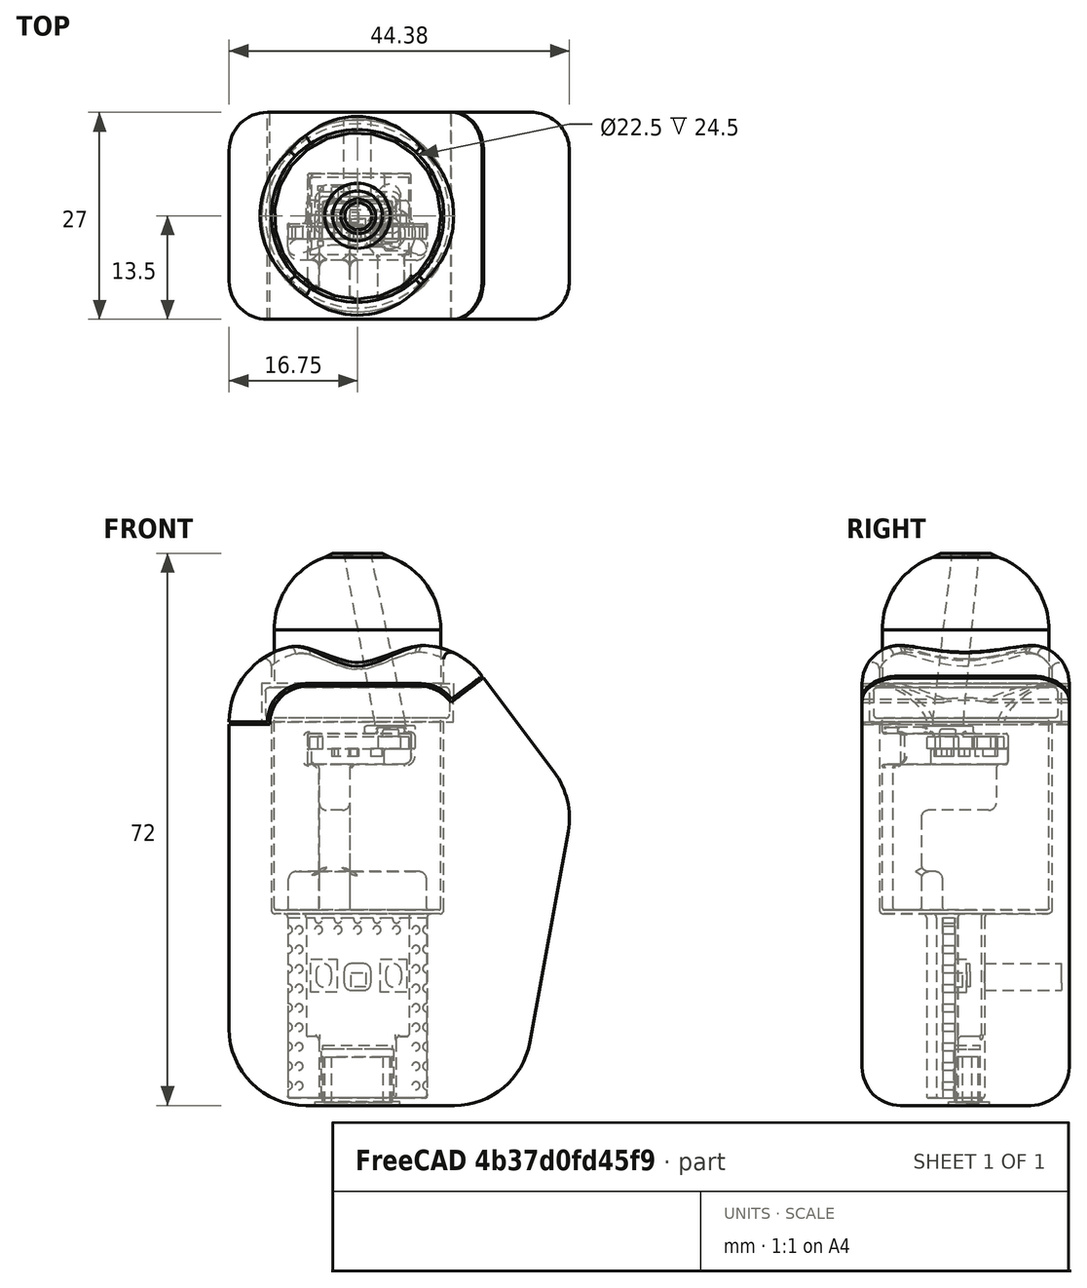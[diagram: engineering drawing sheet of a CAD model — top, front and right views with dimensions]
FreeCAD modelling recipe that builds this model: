
FCSTD DOCUMENT  (FreeCAD 1.0RUnknown)
Label: Device_V7
License: All rights reserved
objects: PartDesign::Fillet×52, Sketcher::SketchObject×37, PartDesign::Pocket×25, PartDesign::Pad×7, PartDesign::SubtractiveLoft×3, PartDesign::Body×3, PartDesign::Revolution×2, Part::Feature×2, PartDesign::SubtractivePipe×1, PartDesign::Groove×1
note: 352 computed .brp shape members not serialized (recipe doc carries the construction recipe); baked Part::Feature solids carry a one-line shape summary decoded from their .brp

FEATURE [Sketcher::SketchObject] Sketch
  ArcFitTolerance = 1e-06
  AttachmentSupport = -> [XZ_Plane]
  FullyConstrained = true
  MakeInternals = false
  MapMode = 5
  Placement = pos=(0,0,0) rot=(1,0,0;1.5708rad)
  sketch-geometry (8):
    g0: LineSegment [constr] StartX=0 StartY=0 StartZ=0 EndX=0 EndY=75 EndZ=0
    g1: LineSegment StartX=0 StartY=75 StartZ=0 EndX=30 EndY=75 EndZ=0
    g2: LineSegment StartX=30 StartY=75 StartZ=0 EndX=45 EndY=55 EndZ=0
    g3: LineSegment [constr] StartX=45 StartY=55 StartZ=0 EndX=35 EndY=0 EndZ=0
    g4: LineSegment [constr] StartX=35 StartY=0 StartZ=0 EndX=0 EndY=0 EndZ=0
    g5: LineSegment StartX=0 StartY=75 StartZ=0 EndX=0 EndY=15 EndZ=0
    g6: LineSegment StartX=0 StartY=15 StartZ=0 EndX=37.7273 EndY=15 EndZ=0
    g7: LineSegment StartX=37.7273 StartY=15 StartZ=0 EndX=45 EndY=55 EndZ=0
  constraints (22):
    c: Coincident(g-1,g0)
    c: Coincident(g0,g1)
    c: Horizontal(g1)
    c: Coincident(g1,g2)
    c: Coincident(g2,g3)
    c: Coincident(g3,g4)
    c: Coincident(g4,g0)
    c: Vertical(g0)
    c: Horizontal(g4)
    c: DistanceX(g4,g4) = 35
    c: DistanceX(g1,g1) = 30
    c: DistanceY(g0,g0) = 75
    c: DistanceY(g2,g1) = 20
    c: DistanceX(g0,g2) = 45
    c: Coincident(g5,g0)
    c: Coincident(g6,g5)
    c: Horizontal(g6)
    c: Coincident(g7,g6)
    c: Coincident(g7,g2)
    c: PointOnObject(g6,g3)
    c: Vertical(g5)
    c: DistanceY(g0,g5) = 15
FEATURE [PartDesign::Pad] Pad
  Direction = (0,-1,2e-16)
  Length = 27
  Length2 = 10
  Midplane = true
  Placement = pos=(0,0,0) rot=(1,0,0;1.5708rad)
  Profile = -> Sketch
  ReferenceAxis = -> Sketch [N_Axis]
  Refine = true
  Suppressed = false
  Type = 0
FEATURE [PartDesign::Fillet] Fillet
  Base = -> Pad [Edge2,Edge5,Edge8,Edge1,Edge11]
  BaseFeature = -> Pad
  Placement = pos=(0,0,0) rot=(1,0,0;1.5708rad)
  Radius = 10
  Refine = true
  SupportTransform = false
  Suppressed = false
  UseAllEdges = false
FEATURE [PartDesign::Fillet] Fillet001
  Base = -> Fillet [Edge19,Edge8]
  BaseFeature = -> Fillet
  Placement = pos=(0,0,0) rot=(1,0,0;1.5708rad)
  Radius = 5
  Refine = true
  SupportTransform = false
  Suppressed = false
  UseAllEdges = false
FEATURE [Sketcher::SketchObject] Sketch003
  ArcFitTolerance = 1e-06
  AttachmentSupport = -> [XZ_Plane001]
  FullyConstrained = true
  MakeInternals = false
  MapMode = 5
  Placement = pos=(0,0,0) rot=(1,0,0;1.5708rad)
  sketch-geometry (9):
    g0: LineSegment StartX=19 StartY=87 StartZ=0 EndX=19 EndY=77 EndZ=0
    g1: LineSegment StartX=19 StartY=77 StartZ=0 EndX=27.6 EndY=77 EndZ=0
    g2: LineSegment StartX=19 StartY=87 StartZ=0 EndX=20 EndY=87 EndZ=0
    g3: LineSegment StartX=20 StartY=87 StartZ=0 EndX=21 EndY=86.5 EndZ=0
    g4: ArcOfCircle CenterX=17.6068 CenterY=77.1 CenterZ=0 NormalX=0 NormalY=0 NormalZ=1 AngleXU=0 Radius=9.99368 StartAngle=6.27318 EndAngle=7.50756
    g5: LineSegment [constr] StartX=0 StartY=0 StartZ=0 EndX=27.6 EndY=0 EndZ=0
    g6: LineSegment [constr] StartX=27.6 StartY=0 StartZ=0 EndX=27.6 EndY=77 EndZ=0
    g7: LineSegment [constr] StartX=27.6 StartY=77 StartZ=0 EndX=0 EndY=77 EndZ=0
    g8: LineSegment [constr] StartX=0 StartY=77 StartZ=0 EndX=0 EndY=0 EndZ=0
  constraints (26):
    c: Vertical(g0)
    c: Coincident(g0,g1)
    c: Horizontal(g1)
    c: Coincident(g0,g2)
    c: Horizontal(g2)
    c: Coincident(g2,g3)
    c: Coincident(g4,g3)
    c: Coincident(g4,g1)
    c: DistanceY(g0,g0) = 10
    c: DistanceY(g3,g2) = 0.5
    c: DistanceX(g2,g2) = 1
    c: DistanceX(g2,g3) = 1
    c: DistanceX(g1,g1) = 8.6
    c: Coincident(g5,g6)
    c: Coincident(g6,g7)
    c: Coincident(g7,g8)
    c: Coincident(g8,g5)
    c: Horizontal(g5)
    c: Horizontal(g7)
    c: Vertical(g6)
    c: Vertical(g8)
    c: Coincident(g5,g-1)
    c: Coincident(g6,g1)
    c: DistanceY(g8,g8) = 77
    c: DistanceX(g7,g7) = 27.6
    c: DistanceY(g0,g4) = 0.1
FEATURE [Sketcher::SketchObject] Sketch004
  ArcFitTolerance = 1e-06
  AttachmentSupport = -> [XZ_Plane001]
  FullyConstrained = true
  MakeInternals = false
  MapMode = 5
  Placement = pos=(0,0,0) rot=(1,0,0;1.5708rad)
  sketch-geometry (7):
    g0: LineSegment StartX=16.75 StartY=87 StartZ=0 EndX=16.75 EndY=77 EndZ=0
    g1: LineSegment [constr] StartX=0 StartY=0 StartZ=0 EndX=27.5 EndY=0 EndZ=0
    g2: LineSegment [constr] StartX=27.5 StartY=0 StartZ=0 EndX=27.5 EndY=77 EndZ=0
    g3: LineSegment [constr] StartX=27.5 StartY=77 StartZ=0 EndX=0 EndY=77 EndZ=0
    g4: LineSegment [constr] StartX=0 StartY=77 StartZ=0 EndX=0 EndY=0 EndZ=0
    g5: GeomPoint [constr] X=10 Y=77 Z=0
    g6: GeomPoint [constr] X=23.5 Y=77 Z=0
  constraints (18):
    c: Vertical(g0)
    c: DistanceY(g0,g0) = 10
    c: Coincident(g1,g2)
    c: Coincident(g2,g3)
    c: Coincident(g3,g4)
    c: Coincident(g4,g1)
    c: Horizontal(g1)
    c: Horizontal(g3)
    c: Vertical(g2)
    c: Vertical(g4)
    c: Coincident(g1,g-1)
    c: DistanceY(g4,g4) = 77
    c: DistanceX(g3,g3) = 27.5
    c: PointOnObject(g5,g3)
    c: PointOnObject(g6,g3)
    c: DistanceX(g6,g2) = 4
    c: DistanceX(g3,g5) = 10
    c: Symmetric(g5,g6,g0)
FEATURE [PartDesign::Revolution] Revolution
  Angle = 360
  Angle2 = 60
  Axis = (0,-2e-16,-1)
  Base = (16.75,1.93e-14,87)
  Placement = pos=(0,0,0) rot=(1,0,0;1.5708rad)
  Profile = -> Sketch003
  ReferenceAxis = -> Sketch004 [Edge1]
  Refine = true
  Reversed = true
  Suppressed = false
  Type = 0
FEATURE [PartDesign::Pad] Pad001
  BaseFeature = -> Revolution
  Direction = (0,-2e-16,-1)
  Length = 36.5
  Length2 = 10
  Placement = pos=(0,0,0) rot=(1,0,0;1.5708rad)
  Profile = -> Revolution [Face2]
  Refine = true
  Suppressed = false
  Type = 0
FEATURE [Sketcher::SketchObject] Sketch006
  ArcFitTolerance = 1e-06
  AttachmentOffset = pos=(0,0,-25) rot=(0,0,1;0rad)
  AttachmentSupport = -> [Fillet001]
  FullyConstrained = true
  MakeInternals = false
  MapMode = 5
  Placement = pos=(0,6.6e-15,40) rot=(1,0,0;3.14159rad)
  sketch-geometry (1):
    g0: Circle CenterX=16.75 CenterY=0 CenterZ=0 NormalX=0 NormalY=0 NormalZ=1 AngleXU=0 Radius=11.25
  constraints (3):
    c: PointOnObject(g0,g-1)
    c: DistanceX(g-1,g0) = 16.75
    c: Diameter(g0) = 22.5
FEATURE [PartDesign::Pocket] Pocket
  BaseFeature = -> Fillet001
  Direction = (0,0,1)
  Length = 5
  Length2 = 5
  Placement = pos=(0,0,0) rot=(1,0,0;1.5708rad)
  Profile = -> Sketch006
  ReferenceAxis = -> Sketch006 [N_Axis]
  Refine = true
  Suppressed = false
  Type = 1
FEATURE [Part::Feature] Part__Feature  label="RP2350-Zero-mini"
  Placement = pos=(7.75,-3,39.5) rot=(1,0,0;4.71239rad)
  shape: bbox 18 x 4.88 x 24.16 mm, 130 faces (baked)
FEATURE [Sketcher::SketchObject] Sketch008
  ArcFitTolerance = 1e-06
  AttachmentSupport = -> [Pocket]
  ExternalGeometry = -> [Pocket]
  FullyConstrained = true
  MakeInternals = false
  MapMode = 5
  Placement = pos=(0,0,40) rot=(0,0,1;3.14159rad)
  sketch-geometry (19):
    g0: LineSegment [constr] StartX=-25.85 StartY=5.5 StartZ=0 EndX=-7.65 EndY=5.5 EndZ=0
    g1: LineSegment StartX=-7.65 StartY=5.5 StartZ=0 EndX=-7.65 EndY=1 EndZ=0
    g2: LineSegment [constr] StartX=-7.65 StartY=1 StartZ=0 EndX=-9.75 EndY=1 EndZ=0
    g3: LineSegment [constr] StartX=-9.75 StartY=1 StartZ=0 EndX=-9.75 EndY=-1.5 EndZ=0
    g4: LineSegment [constr] StartX=-9.75 StartY=-1.5 StartZ=0 EndX=-11.75 EndY=-1.5 EndZ=0
    g5: LineSegment [constr] StartX=-11.75 StartY=-1.5 StartZ=0 EndX=-11.75 EndY=-2.5 EndZ=0
    g6: LineSegment StartX=-11.75 StartY=-2.5 StartZ=0 EndX=-21.75 EndY=-2.5 EndZ=0
    g7: LineSegment [constr] StartX=-21.75 StartY=-2.5 StartZ=0 EndX=-21.75 EndY=-1.5 EndZ=0
    g8: LineSegment [constr] StartX=-21.75 StartY=-1.5 StartZ=0 EndX=-23.75 EndY=-1.5 EndZ=0
    g9: LineSegment [constr] StartX=-23.75 StartY=-1.5 StartZ=0 EndX=-23.75 EndY=1 EndZ=0
    g10: LineSegment [constr] StartX=-23.75 StartY=1 StartZ=0 EndX=-25.85 EndY=1 EndZ=0
    g11: LineSegment StartX=-25.85 StartY=1 StartZ=0 EndX=-25.85 EndY=5.5 EndZ=0
    g12: LineSegment StartX=-25.85 StartY=5.5 StartZ=0 EndX=-20.85 EndY=3.8 EndZ=0
    g13: LineSegment StartX=-20.85 StartY=3.8 StartZ=0 EndX=-12.65 EndY=3.8 EndZ=0
    g14: LineSegment StartX=-12.65 StartY=3.8 StartZ=0 EndX=-7.65 EndY=5.5 EndZ=0
    g15: LineSegment StartX=-25.85 StartY=1 StartZ=0 EndX=-21.75 EndY=1 EndZ=0
    g16: LineSegment StartX=-21.75 StartY=1 StartZ=0 EndX=-21.75 EndY=-2.5 EndZ=0
    g17: LineSegment StartX=-11.75 StartY=-2.5 StartZ=0 EndX=-11.75 EndY=1 EndZ=0
    g18: LineSegment StartX=-11.75 StartY=1 StartZ=0 EndX=-7.65 EndY=1 EndZ=0
  constraints (54):
    c: Horizontal(g0)
    c: Coincident(g0,g1)
    c: Vertical(g1)
    c: Coincident(g1,g2)
    c: Horizontal(g2)
    c: Coincident(g2,g3)
    c: Vertical(g3)
    c: Coincident(g3,g4)
    c: Horizontal(g4)
    c: Coincident(g4,g5)
    c: Vertical(g5)
    c: Coincident(g5,g6)
    c: Horizontal(g6)
    c: Coincident(g6,g7)
    c: Vertical(g7)
    c: Coincident(g7,g8)
    c: Horizontal(g8)
    c: Coincident(g8,g9)
    c: Vertical(g9)
    c: Coincident(g9,g10)
    c: Horizontal(g10)
    c: Coincident(g10,g11)
    c: Vertical(g11)
    c: Coincident(g0,g11)
    c: DistanceX(g0,g-3) = 9.1
    c: DistanceX(g0,g0) = 18.2
    c: DistanceY(g-3,g1) = 1
    c: Horizontal(g2,g9)
    c: DistanceX(g8,g-3) = 7
    c: DistanceX(g-3,g3) = 7
    c: DistanceY(g3,g-3) = 1.5
    c: Horizontal(g3,g7)
    c: DistanceX(g7,g-3) = 5
    c: DistanceX(g-3,g4) = 5
    c: DistanceY(g5,g-3) = 2.5
    c: DistanceY(g-3,g0) = 5.5
    c: Coincident(g0,g12)
    c: Coincident(g12,g13)
    c: Horizontal(g13)
    c: Coincident(g13,g14)
    c: Coincident(g14,g0)
    c: DistanceX(g13,g0) = 5
    c: DistanceX(g0,g12) = 5
    c: DistanceY(g12,g0) = 1.7
    c: Coincident(g15,g10)
    c: Horizontal(g15)
    c: Coincident(g16,g15)
    c: Coincident(g16,g6)
    c: Vertical(g16)
    c: Coincident(g17,g5)
    c: Vertical(g17)
    c: Coincident(g18,g17)
    c: Coincident(g18,g1)
    c: Horizontal(g18)
FEATURE [PartDesign::Pocket] Pocket001
  BaseFeature = -> Pocket
  Direction = (0,0,-1)
  Length = 24
  Length2 = 5
  Placement = pos=(0,0,0) rot=(1,0,0;1.5708rad)
  Profile = -> Sketch008
  ReferenceAxis = -> Sketch008 [N_Axis]
  Refine = true
  Suppressed = false
  Type = 0
FEATURE [Sketcher::SketchObject] Sketch009
  ArcFitTolerance = 1e-06
  AttachmentSupport = -> [Pocket001]
  ExternalGeometry = -> [Pocket001]
  FullyConstrained = true
  MakeInternals = false
  MapMode = 5
  Placement = pos=(0,0,40) rot=(0,0,1;3.14159rad)
  sketch-geometry (8):
    g0: LineSegment StartX=-21.75 StartY=1 StartZ=0 EndX=-23.45 EndY=1 EndZ=0
    g1: LineSegment StartX=-23.45 StartY=1 StartZ=0 EndX=-23.45 EndY=-2 EndZ=0
    g2: LineSegment StartX=-23.45 StartY=-2 StartZ=0 EndX=-21.75 EndY=-2 EndZ=0
    g3: LineSegment StartX=-21.75 StartY=-2 StartZ=0 EndX=-21.75 EndY=1 EndZ=0
    g4: LineSegment StartX=-11.75 StartY=1 StartZ=0 EndX=-11.75 EndY=-2 EndZ=0
    g5: LineSegment StartX=-11.75 StartY=-2 StartZ=0 EndX=-10.05 EndY=-2 EndZ=0
    g6: LineSegment StartX=-10.05 StartY=-2 StartZ=0 EndX=-10.05 EndY=1 EndZ=0
    g7: LineSegment StartX=-10.05 StartY=1 StartZ=0 EndX=-11.75 EndY=1 EndZ=0
  constraints (22):
    c: Coincident(g0,g1)
    c: Coincident(g1,g2)
    c: Coincident(g2,g3)
    c: Coincident(g3,g0)
    c: Horizontal(g0)
    c: Horizontal(g2)
    c: Vertical(g1)
    c: Vertical(g3)
    c: Coincident(g0,g-3)
    c: DistanceY(g1,g1) = 3
    c: DistanceX(g2,g2) = 1.7
    c: Coincident(g4,g5)
    c: Coincident(g5,g6)
    c: Coincident(g6,g7)
    c: Coincident(g7,g4)
    c: Vertical(g4)
    c: Vertical(g6)
    c: Horizontal(g5)
    c: Horizontal(g7)
    c: Coincident(g4,g-4)
    c: Equal(g2,g5)
    c: Equal(g1,g6)
FEATURE [PartDesign::Pocket] Pocket002
  BaseFeature = -> Pocket001
  Direction = (0,0,-1)
  Length = 16
  Length2 = 5
  Placement = pos=(0,0,0) rot=(1,0,0;1.5708rad)
  Profile = -> Sketch009
  ReferenceAxis = -> Sketch009 [N_Axis]
  Refine = true
  Suppressed = false
  Type = 0
FEATURE [Sketcher::SketchObject] Sketch010
  ArcFitTolerance = 1e-06
  AttachmentSupport = -> [Pocket002]
  ExternalGeometry = -> [Pocket002]
  FullyConstrained = true
  MakeInternals = false
  MapMode = 5
  Placement = pos=(0,6.6e-15,15) rot=(1,0,0;3.14159rad)
  sketch-geometry (4):
    g0: LineSegment StartX=12.2 StartY=1.25 StartZ=0 EndX=12.2 EndY=-2.14 EndZ=0
    g1: LineSegment StartX=12.2 StartY=-2.14 StartZ=0 EndX=21.3 EndY=-2.14 EndZ=0
    g2: LineSegment StartX=21.3 StartY=-2.14 StartZ=0 EndX=21.3 EndY=1.25 EndZ=0
    g3: LineSegment StartX=21.3 StartY=1.25 StartZ=0 EndX=12.2 EndY=1.25 EndZ=0
  constraints (12):
    c: Coincident(g0,g1)
    c: Coincident(g1,g2)
    c: Coincident(g2,g3)
    c: Coincident(g3,g0)
    c: Vertical(g0)
    c: Vertical(g2)
    c: Horizontal(g1)
    c: Horizontal(g3)
    c: DistanceY(g2,g2) = 3.39
    c: DistanceX(g3,g3) = 9.1
    c: DistanceX(g-5,g0) = 0.45
    c: DistanceY(g-4,g1) = 0.36
FEATURE [PartDesign::Pocket] Pocket003
  BaseFeature = -> Pocket002
  Direction = (0,0,1)
  Length = 1
  Length2 = 5
  Placement = pos=(0,0,0) rot=(1,0,0;1.5708rad)
  Profile = -> Sketch010
  ReferenceAxis = -> Sketch010 [N_Axis]
  Refine = true
  Suppressed = false
  Type = 0
FEATURE [PartDesign::Fillet] Fillet002
  Base = -> Pocket003 [Edge141,Edge140]
  BaseFeature = -> Pocket003
  Placement = pos=(0,0,0) rot=(1,0,0;1.5708rad)
  Radius = 1
  Refine = true
  SupportTransform = false
  Suppressed = false
  UseAllEdges = false
FEATURE [PartDesign::Fillet] Fillet003
  Base = -> Fillet002 [Edge16,Edge12]
  BaseFeature = -> Fillet002
  Placement = pos=(0,0,0) rot=(1,0,0;1.5708rad)
  Radius = 1
  Refine = true
  SupportTransform = false
  Suppressed = false
  UseAllEdges = false
FEATURE [PartDesign::Fillet] Fillet004
  Base = -> Fillet003 [Edge85,Edge101]
  BaseFeature = -> Fillet003
  Placement = pos=(0,0,0) rot=(1,0,0;1.5708rad)
  Radius = 1
  Refine = true
  SupportTransform = false
  Suppressed = false
  UseAllEdges = false
FEATURE [PartDesign::Fillet] Fillet005
  Base = -> Fillet004 [Edge33,Edge36]
  BaseFeature = -> Fillet004
  Placement = pos=(0,0,0) rot=(1,0,0;1.5708rad)
  Radius = 0.5
  Refine = true
  SupportTransform = false
  Suppressed = false
  UseAllEdges = false
FEATURE [PartDesign::Fillet] Fillet006
  Base = -> Fillet005 [Edge81,Edge76]
  BaseFeature = -> Fillet005
  Placement = pos=(0,0,0) rot=(1,0,0;1.5708rad)
  Radius = 0.5
  Refine = true
  SupportTransform = false
  Suppressed = false
  UseAllEdges = false
FEATURE [PartDesign::Fillet] Fillet007
  Base = -> Fillet006 [Edge2,Edge63]
  BaseFeature = -> Fillet006
  Placement = pos=(0,0,0) rot=(1,0,0;1.5708rad)
  Radius = 0.25
  Refine = true
  SupportTransform = false
  Suppressed = false
  UseAllEdges = false
FEATURE [PartDesign::Fillet] Fillet008
  Base = -> Fillet007 [Edge3,Edge72]
  BaseFeature = -> Fillet007
  Placement = pos=(0,0,0) rot=(1,0,0;1.5708rad)
  Radius = 0.5
  Refine = true
  SupportTransform = false
  Suppressed = false
  UseAllEdges = false
FEATURE [PartDesign::Fillet] Fillet009
  Base = -> Fillet008 [Edge100,Edge29]
  BaseFeature = -> Fillet008
  Placement = pos=(0,0,0) rot=(1,0,0;1.5708rad)
  Radius = 0.13
  Refine = true
  SupportTransform = false
  Suppressed = false
  UseAllEdges = false
FEATURE [Part::Feature] Part__Feature001  label="BME280-5V"
  Placement = pos=(10.5,-5,61.5) rot=(0,0,1;0rad)
  shape: bbox 13 x 10 x 3.53 mm, 88 faces (baked)
FEATURE [Sketcher::SketchObject] Sketch012
  ArcFitTolerance = 1e-06
  AttachmentSupport = -> [XZ_Plane001]
  FullyConstrained = true
  MakeInternals = false
  MapMode = 5
  Placement = pos=(0,0,0) rot=(1,0,0;1.5708rad)
  sketch-geometry (4):
    g0: LineSegment StartX=10.25 StartY=63.5 StartZ=0 EndX=10.25 EndY=59.5 EndZ=0
    g1: LineSegment StartX=10.25 StartY=59.5 StartZ=0 EndX=23.75 EndY=59.5 EndZ=0
    g2: LineSegment StartX=23.75 StartY=59.5 StartZ=0 EndX=23.75 EndY=63.5 EndZ=0
    g3: LineSegment StartX=23.75 StartY=63.5 StartZ=0 EndX=10.25 EndY=63.5 EndZ=0
  constraints (12):
    c: Coincident(g0,g1)
    c: Coincident(g1,g2)
    c: Coincident(g2,g3)
    c: Coincident(g3,g0)
    c: Vertical(g0)
    c: Vertical(g2)
    c: Horizontal(g1)
    c: Horizontal(g3)
    c: Distance(g0,g2) = 13.5
    c: Distance(g1,g3) = 4
    c: DistanceY(g-1,g0) = 59.5
    c: DistanceX(g-1,g0) = 10.25
FEATURE [PartDesign::Pocket] Pocket004
  BaseFeature = -> Pad001
  Direction = (0,1,-2e-16)
  Length = 5.5
  Length2 = 13
  Placement = pos=(0,0,0) rot=(1,0,0;1.5708rad)
  Profile = -> Sketch012
  ReferenceAxis = -> Sketch012 [N_Axis]
  Refine = true
  Suppressed = false
  Type = 4
FEATURE [Sketcher::SketchObject] Sketch013
  ArcFitTolerance = 1e-06
  AttachmentSupport = -> [Pocket004]
  FullyConstrained = true
  MakeInternals = false
  MapMode = 5
  Placement = pos=(0,2.79e-14,63.5) rot=(1,0,0;3.14159rad)
  sketch-geometry (2):
    g0: Circle CenterX=21 CenterY=2.3 CenterZ=0 NormalX=0 NormalY=0 NormalZ=1 AngleXU=0 Radius=2
    g1: Circle CenterX=21 CenterY=2.3 CenterZ=0 NormalX=0 NormalY=0 NormalZ=1 AngleXU=0 Radius=3.3
  constraints (5):
    c: Diameter(g0) = 4
    c: DistanceY(g-1,g0) = 2.3
    c: DistanceX(g-1,g0) = 21
    c: Diameter(g1) = 6.6
    c: Coincident(g1,g0)
FEATURE [Sketcher::SketchObject] Sketch015
  ArcFitTolerance = 1e-06
  AttachmentSupport = -> [Pocket004]
  ExternalGeometry = -> [Pocket004]
  FullyConstrained = true
  MakeInternals = false
  MapMode = 5
  Placement = pos=(0,3.83e-14,87) rot=(0,0,1;3.14159rad)
  sketch-geometry (1):
    g0: Circle CenterX=-16.75 CenterY=0 CenterZ=0 NormalX=0 NormalY=0 NormalZ=1 AngleXU=0 Radius=2.25
  constraints (2):
    c: Coincident(g0,g-3)
    c: Equal(g0,g-3)
FEATURE [PartDesign::Pad] Pad002
  BaseFeature = -> Pocket004
  Direction = (0,0,1)
  Length = 23.5
  Length2 = 10
  Placement = pos=(0,0,0) rot=(1,0,0;1.5708rad)
  Profile = -> Sketch015
  ReferenceAxis = -> Sketch015 [N_Axis]
  Refine = true
  Reversed = true
  Suppressed = false
  Type = 0
FEATURE [PartDesign::Pocket] Pocket005
  BaseFeature = -> Pad002
  Direction = (0,0,1)
  Length = 1
  Length2 = 5
  Placement = pos=(0,0,0) rot=(1,0,0;1.5708rad)
  Profile = -> Sketch013
  ReferenceAxis = -> Sketch013 [N_Axis]
  Refine = true
  Suppressed = false
  Type = 0
FEATURE [Sketcher::SketchObject] Sketch016
  ArcFitTolerance = 1e-06
  AttachmentSupport = -> [Pocket005]
  ExternalGeometry = -> [Pocket005]
  FullyConstrained = true
  MakeInternals = false
  MapMode = 5
  Placement = pos=(0,3.05e-14,63.5) rot=(1,0,0;3.14159rad)
  sketch-geometry (1):
    g0: Circle CenterX=21 CenterY=2.3 CenterZ=0 NormalX=0 NormalY=0 NormalZ=1 AngleXU=0 Radius=2
  constraints (2):
    c: Coincident(g0,g-3)
    c: Equal(g0,g-3)
FEATURE [PartDesign::Pocket] Pocket006
  BaseFeature = -> Pocket005
  Direction = (0,0,1)
  Length = 5
  Length2 = 5
  Placement = pos=(0,0,0) rot=(1,0,0;1.5708rad)
  Profile = -> Sketch016
  ReferenceAxis = -> Sketch016 [N_Axis]
  Refine = true
  Suppressed = false
  Type = 0
FEATURE [Sketcher::SketchObject] Sketch017
  ArcFitTolerance = 1e-06
  AttachmentSupport = -> [XZ_Plane001]
  ExternalGeometry = -> [Pocket006]
  FullyConstrained = true
  MakeInternals = false
  MapMode = 5
  Placement = pos=(0,0,0) rot=(1,0,0;1.5708rad)
  sketch-geometry (7):
    g0: LineSegment StartX=9.25 StartY=75.5 StartZ=0 EndX=9.46286 EndY=70.5 EndZ=0
    g1: LineSegment StartX=15.2301 StartY=70.6227 StartZ=0 EndX=15.2301 EndY=75 EndZ=0
    g2: LineSegment StartX=21 StartY=75 StartZ=0 EndX=21 EndY=68.5 EndZ=0
    g3: ArcOfCircle CenterX=12.3452 CenterY=70.6227 CenterZ=0 NormalX=0 NormalY=0 NormalZ=1 AngleXU=0 Radius=2.88494 StartAngle=3.18414 EndAngle=6.28319
    g4: ArcOfCircle CenterX=18.1151 CenterY=75 CenterZ=0 NormalX=0 NormalY=0 NormalZ=1 AngleXU=0 Radius=2.88494 StartAngle=1.6e-15 EndAngle=3.14159
    g5: ArcOfCircle CenterX=14.9407 CenterY=75.7423 CenterZ=0 NormalX=0 NormalY=0 NormalZ=1 AngleXU=0 Radius=5.69588 StartAngle=1.96559 EndAngle=3.18414
    g6: ArcOfCircle CenterX=10.25 CenterY=87 CenterZ=0 NormalX=0 NormalY=0 NormalZ=1 AngleXU=0 Radius=6.5 StartAngle=5.10718 EndAngle=6.28319
  constraints (18):
    c: Vertical(g1)
    c: Vertical(g2)
    c: Symmetric(g-3,g-3,g2)
    c: Tangent(g3,g0) = -1.5708
    c: Tangent(g3,g1) = -1.5708
    c: Tangent(g4,g1) = 1.5708
    c: Tangent(g4,g2) = 1.5708
    c: Symmetric(g-4,g-4,g6)
    c: Tangent(g6,g5) = 1.5708
    c: DistanceY(g-1,g2) = 75
    c: Perpendicular(g6,g-4)
    c: Tangent(g5,g0) = -1.5708
    c: DistanceY(g5,g6) = 6
    c: DistanceX(g5,g6) = 4
    c: DistanceY(g0,g5) = 5.5
    c: DistanceX(g0,g5) = 3.5
    c: DistanceY(g0,g0) = 5
    c: Equal(g3,g4)
FEATURE [Sketcher::SketchObject] Sketch018
  ArcFitTolerance = 1e-06
  AttachmentSupport = -> [Pocket006]
  ExternalGeometry = -> [Pocket006]
  FullyConstrained = true
  MakeInternals = false
  MapMode = 5
  Placement = pos=(0,3.83e-14,87) rot=(0,0,1;3.14159rad)
  sketch-geometry (1):
    g0: Circle CenterX=-16.75 CenterY=0 CenterZ=0 NormalX=0 NormalY=0 NormalZ=1 AngleXU=0 Radius=1.75
  constraints (2):
    c: Coincident(g0,g-3)
    c: Diameter(g0) = 3.5
FEATURE [PartDesign::SubtractivePipe] SubtractivePipe
  AuxilleryCurvelinear = true
  AuxillerySpineTangent = false
  BaseFeature = -> Pocket006
  Binormal = (0,0,0)
  Mode = 0
  Placement = pos=(0,0,0) rot=(1,0,0;1.5708rad)
  Profile = -> Sketch018
  Refine = true
  Spine = -> Sketch017 [Edge1,Edge2,Edge3,Edge4,Edge5,Edge6]
  SpineTangent = false
  Suppressed = false
  Transformation = 1
  Transition = 0
FEATURE [PartDesign::SubtractiveLoft] SubtractiveLoft
  BaseFeature = -> SubtractivePipe
  Closed = false
  Placement = pos=(0,0,0) rot=(1,0,0;1.5708rad)
  Profile = -> SubtractivePipe [Edge45]
  Refine = true
  Ruled = false
  Sections = -> [SubtractivePipe]
  Suppressed = false
FEATURE [Sketcher::SketchObject] Sketch019
  ArcFitTolerance = 1e-06
  AttachmentSupport = -> [SubtractiveLoft]
  ExternalGeometry = -> [SubtractiveLoft]
  FullyConstrained = true
  MakeInternals = false
  MapMode = 5
  Placement = pos=(0,2.62e-14,59.5) rot=(0,0,1;3.14159rad)
  sketch-geometry (8):
    g0: LineSegment StartX=-23.75 StartY=-5.5 StartZ=0 EndX=-20.25 EndY=-5.5 EndZ=0
    g1: LineSegment StartX=-20.25 StartY=-5.5 StartZ=0 EndX=-20.25 EndY=4.5 EndZ=0
    g2: LineSegment StartX=-20.25 StartY=4.5 StartZ=0 EndX=-23.75 EndY=4.5 EndZ=0
    g3: LineSegment StartX=-23.75 StartY=4.5 StartZ=0 EndX=-23.75 EndY=-5.5 EndZ=0
    g4: LineSegment StartX=-10.25 StartY=-5.5 StartZ=0 EndX=-10.25 EndY=4.5 EndZ=0
    g5: LineSegment StartX=-10.25 StartY=4.5 StartZ=0 EndX=-10.75 EndY=4.5 EndZ=0
    g6: LineSegment StartX=-10.75 StartY=4.5 StartZ=0 EndX=-10.75 EndY=-5.5 EndZ=0
    g7: LineSegment StartX=-10.75 StartY=-5.5 StartZ=0 EndX=-10.25 EndY=-5.5 EndZ=0
  constraints (22):
    c: Coincident(g0,g1)
    c: Coincident(g1,g2)
    c: Coincident(g2,g3)
    c: Coincident(g3,g0)
    c: Horizontal(g0)
    c: Horizontal(g2)
    c: Vertical(g1)
    c: Vertical(g3)
    c: Coincident(g0,g-3)
    c: Coincident(g4,g5)
    c: Coincident(g5,g6)
    c: Coincident(g6,g7)
    c: Coincident(g7,g4)
    c: Vertical(g4)
    c: Vertical(g6)
    c: Horizontal(g5)
    c: Horizontal(g7)
    c: Distance(g4,g6) = 0.5
    c: Coincident(g4,g-3)
    c: Equal(g6,g1)
    c: DistanceY(g4,g4) = 10
    c: DistanceX(g2,g2) = 3.5
FEATURE [PartDesign::Pad] Pad003
  BaseFeature = -> SubtractiveLoft
  Direction = (0,0,1)
  Length = 2
  Length2 = 10
  Placement = pos=(0,0,0) rot=(1,0,0;1.5708rad)
  Profile = -> Sketch019
  ReferenceAxis = -> Sketch019 [N_Axis]
  Refine = true
  Suppressed = false
  Type = 0
FEATURE [Sketcher::SketchObject] Sketch024
  ArcFitTolerance = 1e-06
  AttachmentSupport = -> [XZ_Plane001]
  FullyConstrained = true
  MakeInternals = false
  MapMode = 5
  Placement = pos=(0,0,0) rot=(1,0,0;1.5708rad)
  sketch-geometry (6):
    g0: LineSegment StartX=16.75 StartY=87 StartZ=0 EndX=16.75 EndY=65 EndZ=0
    g1: LineSegment StartX=16.75 StartY=65 StartZ=0 EndX=27.6 EndY=65 EndZ=0
    g2: LineSegment StartX=27.6 StartY=65 StartZ=0 EndX=27.6 EndY=77 EndZ=0
    g3: ArcOfCircle CenterX=17.6068 CenterY=77.1 CenterZ=0 NormalX=0 NormalY=0 NormalZ=1 AngleXU=0 Radius=9.99368 StartAngle=6.27318 EndAngle=7.50756
    g4: LineSegment StartX=20 StartY=87 StartZ=0 EndX=21 EndY=86.5 EndZ=0
    g5: LineSegment StartX=20 StartY=87 StartZ=0 EndX=16.75 EndY=87 EndZ=0
  constraints (15):
    c: Vertical(g0)
    c: Symmetric(g-3,g-3,g0)
    c: Horizontal(g-4,g0)
    c: Coincident(g1,g0)
    c: PointOnObject(g1,g-6)
    c: Horizontal(g1)
    c: Coincident(g2,g1)
    c: Coincident(g-6,g2)
    c: Coincident(g3,g-5)
    c: Coincident(g3,g2)
    c: Equal(g-5,g3)
    c: Coincident(g4,g-3)
    c: Coincident(g4,g3)
    c: Coincident(g5,g4)
    c: Coincident(g5,g0)
FEATURE [PartDesign::Revolution] Revolution001
  Angle = 360
  Angle2 = 60
  Axis = (0,-2e-16,-1)
  Base = (16.75,1.93e-14,87)
  BaseFeature = -> Pad003
  Placement = pos=(0,0,0) rot=(1,0,0;1.5708rad)
  Profile = -> Sketch024
  ReferenceAxis = -> Sketch024 [Edge1]
  Refine = true
  Reversed = true
  Suppressed = false
  Type = 0
FEATURE [Sketcher::SketchObject] Sketch026
  ArcFitTolerance = 1e-06
  AttachmentSupport = -> [Revolution001]
  ExternalGeometry = -> [Revolution001]
  FullyConstrained = true
  MakeInternals = false
  MapMode = 5
  Placement = pos=(0,3.83e-14,87) rot=(0,0,1;3.14159rad)
  sketch-geometry (1):
    g0: Circle CenterX=-16.75 CenterY=0 CenterZ=0 NormalX=0 NormalY=0 NormalZ=1 AngleXU=0 Radius=1.75
  constraints (2):
    c: Coincident(g0,g-3)
    c: Diameter(g0) = 3.5
FEATURE [PartDesign::SubtractiveLoft] SubtractiveLoft001
  BaseFeature = -> Revolution001
  Closed = false
  Placement = pos=(0,0,0) rot=(1,0,0;1.5708rad)
  Profile = -> Revolution001 [Edge44]
  Refine = true
  Ruled = false
  Sections = -> [Sketch026]
  Suppressed = false
FEATURE [Sketcher::SketchObject] Sketch028
  ArcFitTolerance = 1e-06
  AttachmentOffset = pos=(0,0,-4) rot=(0,0,1;0rad)
  AttachmentSupport = -> [XZ_Plane001]
  FullyConstrained = true
  MakeInternals = false
  MapMode = 5
  Placement = pos=(0,4,-9e-16) rot=(1,0,0;1.5708rad)
  sketch-geometry (4):
    g0: LineSegment StartX=11.75 StartY=59.5 StartZ=0 EndX=11.75 EndY=53.5 EndZ=0
    g1: LineSegment StartX=11.75 StartY=53.5 StartZ=0 EndX=15.75 EndY=53.5 EndZ=0
    g2: LineSegment StartX=15.75 StartY=53.5 StartZ=0 EndX=15.75 EndY=59.5 EndZ=0
    g3: LineSegment StartX=15.75 StartY=59.5 StartZ=0 EndX=11.75 EndY=59.5 EndZ=0
  constraints (12):
    c: Coincident(g0,g1)
    c: Coincident(g1,g2)
    c: Coincident(g2,g3)
    c: Coincident(g3,g0)
    c: Vertical(g0)
    c: Vertical(g2)
    c: Horizontal(g1)
    c: Horizontal(g3)
    c: PointOnObject(g0,g-3)
    c: DistanceY(g0,g0) = 6
    c: DistanceX(g1,g1) = 4
    c: Vertical(g-4,g0)
FEATURE [Sketcher::SketchObject] Sketch027
  ArcFitTolerance = 1e-06
  FullyConstrained = true
  MakeInternals = false
  MapMode = 5
  Placement = pos=(0,1.78e-14,40.5) rot=(1,0,0;3.14159rad)
  sketch-geometry (1):
    g0: Circle CenterX=16.75 CenterY=0 CenterZ=0 NormalX=0 NormalY=0 NormalZ=1 AngleXU=0 Radius=2.25
  constraints (3):
    c: PointOnObject(g0,g-1)
    c: Vertical(g0,g-3)
    c: Equal(g0,g-4)
FEATURE [PartDesign::Pad] Pad004
  BaseFeature = -> SubtractiveLoft001
  Direction = (0,-1e-16,-1)
  Length = 19
  Length2 = 10
  Placement = pos=(0,0,0) rot=(1,0,0;1.5708rad)
  Profile = -> Sketch027
  ReferenceAxis = -> Sketch027 [N_Axis]
  Refine = true
  Reversed = true
  Suppressed = false
  Type = 0
FEATURE [PartDesign::Pocket] Pocket008
  BaseFeature = -> Pad004
  Direction = (0,1,-2e-16)
  Length = 15
  Length2 = 5
  Placement = pos=(0,0,0) rot=(1,0,0;1.5708rad)
  Profile = -> Sketch028
  ReferenceAxis = -> Sketch028 [N_Axis]
  Refine = true
  Reversed = true
  Suppressed = false
  Type = 0
FEATURE [PartDesign::Pocket] Pocket009
  BaseFeature = -> Pocket008
  Direction = (0,0,1)
  Length = 3
  Length2 = 5
  Placement = pos=(0,0,0) rot=(1,0,0;1.5708rad)
  Profile = -> Pocket008 [Face23]
  Refine = true
  Reversed = true
  Suppressed = false
  Type = 0
FEATURE [PartDesign::Fillet] Fillet016
  Base = -> Pocket009 [Edge38,Edge43,Edge23]
  BaseFeature = -> Pocket009
  Placement = pos=(0,0,0) rot=(1,0,0;1.5708rad)
  Radius = 0.25
  Refine = true
  SupportTransform = false
  Suppressed = false
  UseAllEdges = false
FEATURE [PartDesign::Fillet] Fillet017
  Base = -> Fillet016 [Edge26]
  BaseFeature = -> Fillet016
  Placement = pos=(0,0,0) rot=(1,0,0;1.5708rad)
  Radius = 1
  Refine = true
  SupportTransform = false
  Suppressed = false
  UseAllEdges = false
FEATURE [PartDesign::Fillet] Fillet018
  Base = -> Fillet017 [Edge32,Edge28,Edge30,Edge65,Edge66,Edge67,Edge45]
  BaseFeature = -> Fillet017
  Placement = pos=(0,0,0) rot=(1,0,0;1.5708rad)
  Radius = 0.125
  Refine = true
  SupportTransform = false
  Suppressed = false
  UseAllEdges = false
FEATURE [PartDesign::Fillet] Fillet019
  Base = -> Fillet018 [Edge28,Edge30,Edge73,Edge74,Edge77,Edge47,Edge49,Edge84,Edge48,Edge79,Edge86]
  BaseFeature = -> Fillet018
  Placement = pos=(0,0,0) rot=(1,0,0;1.5708rad)
  Radius = 0.25
  Refine = true
  SupportTransform = false
  Suppressed = false
  UseAllEdges = false
FEATURE [PartDesign::Fillet] Fillet020
  Base = -> Fillet019 [Edge1]
  BaseFeature = -> Fillet019
  Placement = pos=(0,0,0) rot=(1,0,0;1.5708rad)
  Radius = 0.25
  Refine = true
  SupportTransform = false
  Suppressed = false
  UseAllEdges = false
FEATURE [PartDesign::Fillet] Fillet021
  Base = -> Fillet020 [Edge52]
  BaseFeature = -> Fillet020
  Placement = pos=(0,0,0) rot=(1,0,0;1.5708rad)
  Radius = 1
  Refine = true
  SupportTransform = false
  Suppressed = false
  UseAllEdges = false
FEATURE [Sketcher::SketchObject] Sketch029
  ArcFitTolerance = 1e-06
  AttachmentSupport = -> [Fillet021]
  ExternalGeometry = -> [Fillet021]
  FullyConstrained = true
  MakeInternals = false
  MapMode = 5
  Placement = pos=(0,2.35e-14,53.5) rot=(0,0,1;3.14159rad)
  sketch-geometry (4):
    g0: LineSegment StartX=-15.75 StartY=10.8038 StartZ=0 EndX=-15.75 EndY=5.80382 EndZ=0
    g1: LineSegment StartX=-15.75 StartY=5.80382 StartZ=0 EndX=-11.75 EndY=5.80382 EndZ=0
    g2: LineSegment StartX=-11.75 StartY=5.80382 StartZ=0 EndX=-11.75 EndY=10.8038 EndZ=0
    g3: LineSegment StartX=-11.75 StartY=10.8038 StartZ=0 EndX=-15.75 EndY=10.8038 EndZ=0
  constraints (11):
    c: Coincident(g0,g1)
    c: Coincident(g1,g2)
    c: Coincident(g2,g3)
    c: Coincident(g3,g0)
    c: Vertical(g0)
    c: Vertical(g2)
    c: Horizontal(g1)
    c: Horizontal(g3)
    c: Coincident(g0,g-3)
    c: Vertical(g2,g-3)
    c: DistanceY(g2,g2) = 5
FEATURE [PartDesign::Pocket] Pocket010
  BaseFeature = -> Fillet021
  Direction = (0,0,-1)
  Length = 17
  Length2 = 5
  Placement = pos=(0,0,0) rot=(1,0,0;1.5708rad)
  Profile = -> Sketch029
  ReferenceAxis = -> Sketch029 [N_Axis]
  Refine = true
  Suppressed = false
  Type = 0
FEATURE [PartDesign::Fillet] Fillet022
  Base = -> Pocket010 [Edge22]
  BaseFeature = -> Pocket010
  Placement = pos=(0,0,0) rot=(1,0,0;1.5708rad)
  Radius = 1
  Refine = true
  SupportTransform = false
  Suppressed = false
  UseAllEdges = false
FEATURE [PartDesign::Fillet] Fillet010
  Base = -> Fillet009 [Edge70,Edge66]
  BaseFeature = -> Fillet009
  Placement = pos=(0,0,0) rot=(1,0,0;1.5708rad)
  Radius = 10
  Refine = true
  SupportTransform = false
  Suppressed = false
  UseAllEdges = false
FEATURE [PartDesign::Fillet] Fillet011
  Base = -> Fillet010 [Edge29,Edge46]
  BaseFeature = -> Fillet010
  Placement = pos=(0,0,0) rot=(1,0,0;1.5708rad)
  Radius = 1
  Refine = true
  SupportTransform = false
  Suppressed = false
  UseAllEdges = false
FEATURE [PartDesign::Fillet] Fillet012
  Base = -> Fillet011 [Edge16]
  BaseFeature = -> Fillet011
  Placement = pos=(0,0,0) rot=(1,0,0;1.5708rad)
  Radius = 0.25
  Refine = true
  SupportTransform = false
  Suppressed = false
  UseAllEdges = false
FEATURE [PartDesign::Fillet] Fillet013
  Base = -> Fillet012 [Edge82]
  BaseFeature = -> Fillet012
  Placement = pos=(0,0,0) rot=(1,0,0;1.5708rad)
  Radius = 0.5
  Refine = true
  SupportTransform = false
  Suppressed = false
  UseAllEdges = false
FEATURE [PartDesign::Fillet] Fillet014
  Base = -> Fillet013 [Edge54]
  BaseFeature = -> Fillet013
  Placement = pos=(0,0,0) rot=(1,0,0;1.5708rad)
  Radius = 0.5
  Refine = true
  SupportTransform = false
  Suppressed = false
  UseAllEdges = false
FEATURE [PartDesign::Fillet] Fillet015
  Base = -> Fillet014 [Edge82]
  BaseFeature = -> Fillet014
  Placement = pos=(0,0,0) rot=(1,0,0;1.5708rad)
  Radius = 0.9
  Refine = true
  SupportTransform = false
  Suppressed = false
  UseAllEdges = false
FEATURE [Sketcher::SketchObject] Sketch021
  ArcFitTolerance = 1e-06
  AttachmentSupport = -> [Fillet015]
  ExternalGeometry = -> [Fillet015]
  FullyConstrained = true
  MakeInternals = false
  MapMode = 5
  Placement = pos=(0,6.6e-15,15) rot=(1,0,0;3.14159rad)
  sketch-geometry (10):
    g0: LineSegment StartX=12.2 StartY=-3.14 StartZ=0 EndX=21.3 EndY=-3.14 EndZ=0
    g1: LineSegment StartX=22.3 StartY=-2.14 StartZ=0 EndX=22.3 EndY=1.25 EndZ=0
    g2: LineSegment StartX=21.3 StartY=2.25 StartZ=0 EndX=12.2 EndY=2.25 EndZ=0
    g3: LineSegment StartX=11.2 StartY=1.25 StartZ=0 EndX=11.2 EndY=-2.14 EndZ=0
    g4: ArcOfCircle CenterX=12.2 CenterY=-2.14 CenterZ=0 NormalX=0 NormalY=0 NormalZ=1 AngleXU=0 Radius=1 StartAngle=3.14159 EndAngle=4.71239
    g5: ArcOfCircle CenterX=21.3 CenterY=-2.14 CenterZ=0 NormalX=0 NormalY=0 NormalZ=1 AngleXU=0 Radius=1 StartAngle=4.71239 EndAngle=6.28319
    g6: ArcOfCircle CenterX=21.3 CenterY=1.25 CenterZ=0 NormalX=0 NormalY=0 NormalZ=1 AngleXU=0 Radius=1 StartAngle=0 EndAngle=1.5708
    g7: ArcOfCircle CenterX=12.2 CenterY=1.25 CenterZ=0 NormalX=0 NormalY=0 NormalZ=1 AngleXU=0 Radius=1 StartAngle=1.5708 EndAngle=3.14159
    g8: GeomPoint [constr] X=11.2 Y=-3.14 Z=0
    g9: GeomPoint [constr] X=22.3 Y=2.25 Z=0
  constraints (24):
    c: Tangent(g0,g4) = -1.5708
    c: Tangent(g0,g5) = -1.5708
    c: Tangent(g1,g5) = -1.5708
    c: Tangent(g1,g6) = -1.5708
    c: Tangent(g2,g6) = -1.5708
    c: Tangent(g2,g7) = -1.5708
    c: Tangent(g3,g7) = -1.5708
    c: Tangent(g3,g4) = -1.5708
    c: Horizontal(g0)
    c: Horizontal(g2)
    c: Vertical(g1)
    c: Vertical(g3)
    c: Equal(g4,g5)
    c: Equal(g5,g6)
    c: Equal(g6,g7)
    c: PointOnObject(g8,g0)
    c: PointOnObject(g8,g3)
    c: PointOnObject(g9,g1)
    c: PointOnObject(g9,g2)
    c: Radius(g5) = 1
    c: DistanceY(g-3,g2) = 1
    c: DistanceX(g3,g-5) = 1
    c: DistanceX(g-6,g1) = 1
    c: DistanceY(g0,g-4) = 1
FEATURE [PartDesign::Pocket] Pocket007
  BaseFeature = -> Fillet015
  Direction = (0,0,1)
  Length = 0.5
  Length2 = 5
  Placement = pos=(0,0,0) rot=(1,0,0;1.5708rad)
  Profile = -> Sketch021
  ReferenceAxis = -> Sketch021 [N_Axis]
  Refine = true
  Suppressed = false
  Type = 0
FEATURE [Sketcher::SketchObject] Sketch030
  ArcFitTolerance = 1e-06
  AttachmentSupport = -> [Fillet022]
  ExternalGeometry = -> [Fillet022]
  FullyConstrained = true
  MakeInternals = false
  MapMode = 5
  Placement = pos=(0,1.78e-14,40.5) rot=(1,0,0;3.14159rad)
  sketch-geometry (4):
    g0: LineSegment StartX=7.75 StartY=5.80382 StartZ=0 EndX=7.75 EndY=3 EndZ=0
    g1: LineSegment StartX=7.75 StartY=3 StartZ=0 EndX=25.75 EndY=3 EndZ=0
    g2: LineSegment StartX=25.75 StartY=3 StartZ=0 EndX=25.75 EndY=5.80382 EndZ=0
    g3: LineSegment StartX=25.75 StartY=5.80382 StartZ=0 EndX=7.75 EndY=5.80382 EndZ=0
  constraints (12):
    c: Coincident(g0,g1)
    c: Coincident(g1,g2)
    c: Coincident(g2,g3)
    c: Coincident(g3,g0)
    c: Vertical(g0)
    c: Vertical(g2)
    c: Horizontal(g1)
    c: Horizontal(g3)
    c: PointOnObject(g-3,g3)
    c: DistanceX(g3,g3) = 18
    c: DistanceX(g0,g-3) = 4
    c: DistanceY(g-1,g1) = 3
FEATURE [PartDesign::Pocket] Pocket011
  BaseFeature = -> Fillet022
  Direction = (0,0,1)
  Length = 5
  Length2 = 5
  Placement = pos=(0,0,0) rot=(1,0,0;1.5708rad)
  Profile = -> Sketch030
  ReferenceAxis = -> Sketch030 [N_Axis]
  Refine = true
  Suppressed = false
  Type = 0
FEATURE [PartDesign::Fillet] Fillet023
  Base = -> Pocket011 [Edge54,Edge26,Edge59,Edge60]
  BaseFeature = -> Pocket011
  Placement = pos=(0,0,0) rot=(1,0,0;1.5708rad)
  Radius = 1.4
  Refine = true
  SupportTransform = false
  Suppressed = false
  UseAllEdges = false
FEATURE [PartDesign::Fillet] Fillet024
  Base = -> Fillet023 [Edge30]
  BaseFeature = -> Fillet023
  Placement = pos=(0,0,0) rot=(1,0,0;1.5708rad)
  Radius = 1
  Refine = true
  SupportTransform = false
  Suppressed = false
  UseAllEdges = false
FEATURE [PartDesign::Fillet] Fillet025
  Base = -> Fillet024 [Edge35]
  BaseFeature = -> Fillet024
  Placement = pos=(0,0,0) rot=(1,0,0;1.5708rad)
  Radius = 1
  Refine = true
  SupportTransform = false
  Suppressed = false
  UseAllEdges = false
FEATURE [PartDesign::Fillet] Fillet026
  Base = -> Fillet025 [Edge64,Edge12,Edge6,Edge1]
  BaseFeature = -> Fillet025
  Placement = pos=(0,0,0) rot=(1,0,0;1.5708rad)
  Radius = 1
  Refine = true
  SupportTransform = false
  Suppressed = false
  UseAllEdges = false
FEATURE [PartDesign::Fillet] Fillet027
  Base = -> Fillet026 [Edge46,Edge5]
  BaseFeature = -> Fillet026
  Placement = pos=(0,0,0) rot=(1,0,0;1.5708rad)
  Radius = 0.5
  Refine = true
  SupportTransform = false
  Suppressed = false
  UseAllEdges = false
FEATURE [Sketcher::SketchObject] Sketch031
  ArcFitTolerance = 1e-06
  AttachmentSupport = -> [XZ_Plane002]
  FullyConstrained = true
  MakeInternals = false
  MapMode = 5
  Placement = pos=(0,0,0) rot=(1,0,0;1.5708rad)
  sketch-geometry (8):
    g0: LineSegment [constr] StartX=0 StartY=0 StartZ=0 EndX=0 EndY=75 EndZ=0
    g1: LineSegment StartX=0 StartY=75 StartZ=0 EndX=30 EndY=75 EndZ=0
    g2: LineSegment StartX=30 StartY=75 StartZ=0 EndX=45 EndY=55 EndZ=0
    g3: LineSegment [constr] StartX=45 StartY=55 StartZ=0 EndX=35 EndY=0 EndZ=0
    g4: LineSegment [constr] StartX=35 StartY=0 StartZ=0 EndX=0 EndY=0 EndZ=0
    g5: LineSegment StartX=0 StartY=75 StartZ=0 EndX=0 EndY=15 EndZ=0
    g6: LineSegment StartX=0 StartY=15 StartZ=0 EndX=37.7273 EndY=15 EndZ=0
    g7: LineSegment StartX=37.7273 StartY=15 StartZ=0 EndX=45 EndY=55 EndZ=0
  constraints (22):
    c: Coincident(g-1,g0)
    c: Coincident(g0,g1)
    c: Horizontal(g1)
    c: Coincident(g1,g2)
    c: Coincident(g2,g3)
    c: Coincident(g3,g4)
    c: Coincident(g4,g0)
    c: Vertical(g0)
    c: Horizontal(g4)
    c: DistanceX(g4,g4) = 35
    c: DistanceX(g1,g1) = 30
    c: DistanceY(g0,g0) = 75
    c: DistanceY(g2,g1) = 20
    c: DistanceX(g0,g2) = 45
    c: Coincident(g5,g0)
    c: Coincident(g6,g5)
    c: Horizontal(g6)
    c: Coincident(g7,g6)
    c: Coincident(g7,g2)
    c: PointOnObject(g6,g3)
    c: Vertical(g5)
    c: DistanceY(g0,g5) = 15
FEATURE [PartDesign::Pad] Pad005
  Direction = (0,-1,2e-16)
  Length = 27
  Length2 = 10
  Midplane = true
  Placement = pos=(0,0,0) rot=(1,0,0;1.5708rad)
  Profile = -> Sketch031
  ReferenceAxis = -> Sketch031 [N_Axis]
  Refine = true
  Suppressed = false
  Type = 0
FEATURE [PartDesign::Fillet] Fillet032
  Base = -> Pad005 [Edge2,Edge5,Edge8,Edge1,Edge11]
  BaseFeature = -> Pad005
  Placement = pos=(0,0,0) rot=(1,0,0;1.5708rad)
  Radius = 10
  Refine = true
  SupportTransform = false
  Suppressed = false
  UseAllEdges = false
FEATURE [PartDesign::Fillet] Fillet033
  Base = -> Fillet032 [Edge19,Edge8]
  BaseFeature = -> Fillet032
  Placement = pos=(0,0,0) rot=(1,0,0;1.5708rad)
  Radius = 5
  Refine = true
  SupportTransform = false
  Suppressed = false
  UseAllEdges = false
FEATURE [Sketcher::SketchObject] Sketch032
  ArcFitTolerance = 1e-06
  AttachmentOffset = pos=(0,0,-25) rot=(0,0,1;0rad)
  AttachmentSupport = -> [Fillet033]
  FullyConstrained = true
  MakeInternals = false
  MapMode = 5
  Placement = pos=(0,6.6e-15,40) rot=(1,0,0;3.14159rad)
  sketch-geometry (1):
    g0: Circle CenterX=16.75 CenterY=0 CenterZ=0 NormalX=0 NormalY=0 NormalZ=1 AngleXU=0 Radius=11.25
  constraints (3):
    c: PointOnObject(g0,g-1)
    c: DistanceX(g-1,g0) = 16.75
    c: Diameter(g0) = 22.5
FEATURE [PartDesign::Pocket] Pocket012
  BaseFeature = -> Fillet033
  Direction = (0,0,1)
  Length = 5
  Length2 = 5
  Placement = pos=(0,0,0) rot=(1,0,0;1.5708rad)
  Profile = -> Sketch032
  ReferenceAxis = -> Sketch032 [N_Axis]
  Refine = true
  Suppressed = false
  Type = 1
FEATURE [Sketcher::SketchObject] Sketch033
  ArcFitTolerance = 1e-06
  AttachmentSupport = -> [Pocket012]
  ExternalGeometry = -> [Pocket012]
  FullyConstrained = true
  MakeInternals = false
  MapMode = 5
  Placement = pos=(0,0,40) rot=(0,0,1;3.14159rad)
  sketch-geometry (19):
    g0: LineSegment [constr] StartX=-25.85 StartY=5.5 StartZ=0 EndX=-7.65 EndY=5.5 EndZ=0
    g1: LineSegment StartX=-7.65 StartY=5.5 StartZ=0 EndX=-7.65 EndY=1.3 EndZ=0
    g2: LineSegment [constr] StartX=-7.65 StartY=1.3 StartZ=0 EndX=-9.75 EndY=1.3 EndZ=0
    g3: LineSegment [constr] StartX=-9.75 StartY=1.3 StartZ=0 EndX=-9.75 EndY=-1.5 EndZ=0
    g4: LineSegment [constr] StartX=-9.75 StartY=-1.5 StartZ=0 EndX=-11.75 EndY=-1.5 EndZ=0
    g5: LineSegment [constr] StartX=-11.75 StartY=-1.5 StartZ=0 EndX=-11.75 EndY=-2.5 EndZ=0
    g6: LineSegment StartX=-11.75 StartY=-2.5 StartZ=0 EndX=-21.75 EndY=-2.5 EndZ=0
    g7: LineSegment [constr] StartX=-21.75 StartY=-2.5 StartZ=0 EndX=-21.75 EndY=-1.5 EndZ=0
    g8: LineSegment [constr] StartX=-21.75 StartY=-1.5 StartZ=0 EndX=-23.75 EndY=-1.5 EndZ=0
    g9: LineSegment [constr] StartX=-23.75 StartY=-1.5 StartZ=0 EndX=-23.75 EndY=1.3 EndZ=0
    g10: LineSegment [constr] StartX=-23.75 StartY=1.3 StartZ=0 EndX=-25.85 EndY=1.3 EndZ=0
    g11: LineSegment StartX=-25.85 StartY=1.3 StartZ=0 EndX=-25.85 EndY=5.5 EndZ=0
    g12: LineSegment StartX=-25.85 StartY=5.5 StartZ=0 EndX=-20.85 EndY=3.5 EndZ=0
    g13: LineSegment StartX=-20.85 StartY=3.5 StartZ=0 EndX=-12.65 EndY=3.5 EndZ=0
    g14: LineSegment StartX=-12.65 StartY=3.5 StartZ=0 EndX=-7.65 EndY=5.5 EndZ=0
    g15: LineSegment StartX=-25.85 StartY=1.3 StartZ=0 EndX=-21.75 EndY=1.3 EndZ=0
    g16: LineSegment StartX=-21.75 StartY=1.3 StartZ=0 EndX=-21.75 EndY=-2.5 EndZ=0
    g17: LineSegment StartX=-11.75 StartY=-2.5 StartZ=0 EndX=-11.75 EndY=1.3 EndZ=0
    g18: LineSegment StartX=-11.75 StartY=1.3 StartZ=0 EndX=-7.65 EndY=1.3 EndZ=0
  constraints (54):
    c: Horizontal(g0)
    c: Coincident(g0,g1)
    c: Vertical(g1)
    c: Coincident(g1,g2)
    c: Horizontal(g2)
    c: Coincident(g2,g3)
    c: Vertical(g3)
    c: Coincident(g3,g4)
    c: Horizontal(g4)
    c: Coincident(g4,g5)
    c: Vertical(g5)
    c: Coincident(g5,g6)
    c: Horizontal(g6)
    c: Coincident(g6,g7)
    c: Vertical(g7)
    c: Coincident(g7,g8)
    c: Horizontal(g8)
    c: Coincident(g8,g9)
    c: Vertical(g9)
    c: Coincident(g9,g10)
    c: Horizontal(g10)
    c: Coincident(g10,g11)
    c: Vertical(g11)
    c: Coincident(g0,g11)
    c: DistanceX(g0,g-3) = 9.1
    c: DistanceX(g0,g0) = 18.2
    c: DistanceY(g-3,g1) = 1.3
    c: Horizontal(g2,g9)
    c: DistanceX(g8,g-3) = 7
    c: DistanceX(g-3,g3) = 7
    c: DistanceY(g3,g-3) = 1.5
    c: Horizontal(g3,g7)
    c: DistanceX(g7,g-3) = 5
    c: DistanceX(g-3,g4) = 5
    c: DistanceY(g5,g-3) = 2.5
    c: DistanceY(g-3,g0) = 5.5
    c: Coincident(g0,g12)
    c: Coincident(g12,g13)
    c: Horizontal(g13)
    c: Coincident(g13,g14)
    c: Coincident(g14,g0)
    c: DistanceX(g13,g0) = 5
    c: DistanceX(g0,g12) = 5
    c: DistanceY(g12,g0) = 2
    c: Coincident(g15,g10)
    c: Horizontal(g15)
    c: Coincident(g16,g15)
    c: Coincident(g16,g6)
    c: Vertical(g16)
    c: Coincident(g17,g5)
    c: Vertical(g17)
    c: Coincident(g18,g17)
    c: Coincident(g18,g1)
    c: Horizontal(g18)
FEATURE [PartDesign::Pocket] Pocket013
  BaseFeature = -> Pocket012
  Direction = (0,0,-1)
  Length = 24
  Length2 = 5
  Placement = pos=(0,0,0) rot=(1,0,0;1.5708rad)
  Profile = -> Sketch033
  ReferenceAxis = -> Sketch033 [N_Axis]
  Refine = true
  Suppressed = false
  Type = 0
FEATURE [Sketcher::SketchObject] Sketch034
  ArcFitTolerance = 1e-06
  AttachmentSupport = -> [Pocket013]
  ExternalGeometry = -> [Pocket013]
  FullyConstrained = true
  MakeInternals = false
  MapMode = 5
  Placement = pos=(0,0,40) rot=(0,0,1;3.14159rad)
  sketch-geometry (8):
    g0: LineSegment StartX=-21.75 StartY=1.3 StartZ=0 EndX=-23.45 EndY=1.3 EndZ=0
    g1: LineSegment StartX=-23.45 StartY=1.3 StartZ=0 EndX=-23.45 EndY=-1.7 EndZ=0
    g2: LineSegment StartX=-23.45 StartY=-1.7 StartZ=0 EndX=-21.75 EndY=-1.7 EndZ=0
    g3: LineSegment StartX=-21.75 StartY=-1.7 StartZ=0 EndX=-21.75 EndY=1.3 EndZ=0
    g4: LineSegment StartX=-11.75 StartY=1.3 StartZ=0 EndX=-11.75 EndY=-1.7 EndZ=0
    g5: LineSegment StartX=-11.75 StartY=-1.7 StartZ=0 EndX=-10.05 EndY=-1.7 EndZ=0
    g6: LineSegment StartX=-10.05 StartY=-1.7 StartZ=0 EndX=-10.05 EndY=1.3 EndZ=0
    g7: LineSegment StartX=-10.05 StartY=1.3 StartZ=0 EndX=-11.75 EndY=1.3 EndZ=0
  constraints (22):
    c: Coincident(g0,g1)
    c: Coincident(g1,g2)
    c: Coincident(g2,g3)
    c: Coincident(g3,g0)
    c: Horizontal(g0)
    c: Horizontal(g2)
    c: Vertical(g1)
    c: Vertical(g3)
    c: Coincident(g0,g-3)
    c: DistanceY(g1,g1) = 3
    c: DistanceX(g2,g2) = 1.7
    c: Coincident(g4,g5)
    c: Coincident(g5,g6)
    c: Coincident(g6,g7)
    c: Coincident(g7,g4)
    c: Vertical(g4)
    c: Vertical(g6)
    c: Horizontal(g5)
    c: Horizontal(g7)
    c: Coincident(g4,g-4)
    c: Equal(g2,g5)
    c: Equal(g1,g6)
FEATURE [PartDesign::Pocket] Pocket014
  BaseFeature = -> Pocket013
  Direction = (0,0,-1)
  Length = 16
  Length2 = 5
  Placement = pos=(0,0,0) rot=(1,0,0;1.5708rad)
  Profile = -> Sketch034
  ReferenceAxis = -> Sketch034 [N_Axis]
  Refine = true
  Suppressed = false
  Type = 0
FEATURE [Sketcher::SketchObject] Sketch035
  ArcFitTolerance = 1e-06
  AttachmentSupport = -> [Pocket014]
  ExternalGeometry = -> [Pocket014]
  FullyConstrained = true
  MakeInternals = false
  MapMode = 5
  Placement = pos=(0,6.6e-15,15) rot=(1,0,0;3.14159rad)
  sketch-geometry (4):
    g0: LineSegment StartX=12.2 StartY=1.45 StartZ=0 EndX=12.2 EndY=-1.94 EndZ=0
    g1: LineSegment StartX=12.2 StartY=-1.94 StartZ=0 EndX=21.3 EndY=-1.94 EndZ=0
    g2: LineSegment StartX=21.3 StartY=-1.94 StartZ=0 EndX=21.3 EndY=1.45 EndZ=0
    g3: LineSegment StartX=21.3 StartY=1.45 StartZ=0 EndX=12.2 EndY=1.45 EndZ=0
  constraints (12):
    c: Coincident(g0,g1)
    c: Coincident(g1,g2)
    c: Coincident(g2,g3)
    c: Coincident(g3,g0)
    c: Vertical(g0)
    c: Vertical(g2)
    c: Horizontal(g1)
    c: Horizontal(g3)
    c: DistanceY(g2,g2) = 3.39
    c: DistanceX(g3,g3) = 9.1
    c: DistanceX(g-5,g0) = 0.45
    c: DistanceY(g-4,g1) = 0.56
FEATURE [PartDesign::Pocket] Pocket015
  BaseFeature = -> Pocket014
  Direction = (0,0,1)
  Length = 1
  Length2 = 5
  Placement = pos=(0,0,0) rot=(1,0,0;1.5708rad)
  Profile = -> Sketch035
  ReferenceAxis = -> Sketch035 [N_Axis]
  Refine = true
  Suppressed = false
  Type = 0
FEATURE [PartDesign::Fillet] Fillet034
  Base = -> Pocket015 [Edge141,Edge140]
  BaseFeature = -> Pocket015
  Placement = pos=(0,0,0) rot=(1,0,0;1.5708rad)
  Radius = 1
  Refine = true
  SupportTransform = false
  Suppressed = false
  UseAllEdges = false
FEATURE [PartDesign::Fillet] Fillet035
  Base = -> Fillet034 [Edge16,Edge12]
  BaseFeature = -> Fillet034
  Placement = pos=(0,0,0) rot=(1,0,0;1.5708rad)
  Radius = 1
  Refine = true
  SupportTransform = false
  Suppressed = false
  UseAllEdges = false
FEATURE [PartDesign::Fillet] Fillet036
  Base = -> Fillet035 [Edge85,Edge101]
  BaseFeature = -> Fillet035
  Placement = pos=(0,0,0) rot=(1,0,0;1.5708rad)
  Radius = 1
  Refine = true
  SupportTransform = false
  Suppressed = false
  UseAllEdges = false
FEATURE [PartDesign::Fillet] Fillet037
  Base = -> Fillet036 [Edge33,Edge36]
  BaseFeature = -> Fillet036
  Placement = pos=(0,0,0) rot=(1,0,0;1.5708rad)
  Radius = 0.5
  Refine = true
  SupportTransform = false
  Suppressed = false
  UseAllEdges = false
FEATURE [PartDesign::Fillet] Fillet038
  Base = -> Fillet037 [Edge85,Edge82]
  BaseFeature = -> Fillet037
  Placement = pos=(0,0,0) rot=(1,0,0;1.5708rad)
  Radius = 0.5
  Refine = true
  SupportTransform = false
  Suppressed = false
  UseAllEdges = false
FEATURE [PartDesign::Fillet] Fillet039
  Base = -> Fillet038 [Edge24,Edge56]
  BaseFeature = -> Fillet038
  Placement = pos=(0,0,0) rot=(1,0,0;1.5708rad)
  Radius = 0.25
  Refine = true
  SupportTransform = false
  Suppressed = false
  UseAllEdges = false
FEATURE [PartDesign::Fillet] Fillet040
  Base = -> Fillet039 [Edge38,Edge95]
  BaseFeature = -> Fillet039
  Placement = pos=(0,0,0) rot=(1,0,0;1.5708rad)
  Radius = 0.5
  Refine = true
  SupportTransform = false
  Suppressed = false
  UseAllEdges = false
FEATURE [PartDesign::Fillet] Fillet041
  Base = -> Fillet040 [Edge79,Edge60]
  BaseFeature = -> Fillet040
  Placement = pos=(0,0,0) rot=(1,0,0;1.5708rad)
  Radius = 0.13
  Refine = true
  SupportTransform = false
  Suppressed = false
  UseAllEdges = false
FEATURE [PartDesign::Fillet] Fillet042
  Base = -> Fillet041 [Edge42,Edge38]
  BaseFeature = -> Fillet041
  Placement = pos=(0,0,0) rot=(1,0,0;1.5708rad)
  Radius = 10
  Refine = true
  SupportTransform = false
  Suppressed = false
  UseAllEdges = false
FEATURE [PartDesign::Fillet] Fillet043
  Base = -> Fillet042 [Edge27,Edge44]
  BaseFeature = -> Fillet042
  Placement = pos=(0,0,0) rot=(1,0,0;1.5708rad)
  Radius = 1
  Refine = true
  SupportTransform = false
  Suppressed = false
  UseAllEdges = false
FEATURE [PartDesign::Fillet] Fillet044
  Base = -> Fillet043 [Edge80]
  BaseFeature = -> Fillet043
  Placement = pos=(0,0,0) rot=(1,0,0;1.5708rad)
  Radius = 0.25
  Refine = true
  SupportTransform = false
  Suppressed = false
  UseAllEdges = false
FEATURE [PartDesign::Fillet] Fillet045
  Base = -> Fillet044 [Edge30]
  BaseFeature = -> Fillet044
  Placement = pos=(0,0,0) rot=(1,0,0;1.5708rad)
  Radius = 0.5
  Refine = true
  SupportTransform = false
  Suppressed = false
  UseAllEdges = false
FEATURE [PartDesign::Fillet] Fillet046
  Base = -> Fillet045 [Edge44]
  BaseFeature = -> Fillet045
  Placement = pos=(0,0,0) rot=(1,0,0;1.5708rad)
  Radius = 0.5
  Refine = true
  SupportTransform = false
  Suppressed = false
  UseAllEdges = false
FEATURE [PartDesign::Fillet] Fillet047
  Base = -> Fillet046 [Edge82]
  BaseFeature = -> Fillet046
  Placement = pos=(0,0,0) rot=(1,0,0;1.5708rad)
  Radius = 0.9
  Refine = true
  SupportTransform = false
  Suppressed = false
  UseAllEdges = false
FEATURE [Sketcher::SketchObject] Sketch036
  ArcFitTolerance = 1e-06
  AttachmentSupport = -> [Fillet047]
  ExternalGeometry = -> [Fillet047]
  FullyConstrained = true
  MakeInternals = false
  MapMode = 5
  Placement = pos=(0,6.6e-15,15) rot=(1,0,0;3.14159rad)
  sketch-geometry (10):
    g0: LineSegment StartX=12.2 StartY=-2.94 StartZ=0 EndX=21.3 EndY=-2.94 EndZ=0
    g1: LineSegment StartX=22.3 StartY=-1.94 StartZ=0 EndX=22.3 EndY=1.45 EndZ=0
    g2: LineSegment StartX=21.3 StartY=2.45 StartZ=0 EndX=12.2 EndY=2.45 EndZ=0
    g3: LineSegment StartX=11.2 StartY=1.45 StartZ=0 EndX=11.2 EndY=-1.94 EndZ=0
    g4: ArcOfCircle CenterX=12.2 CenterY=-1.94 CenterZ=0 NormalX=0 NormalY=0 NormalZ=1 AngleXU=0 Radius=1 StartAngle=3.14159 EndAngle=4.71239
    g5: ArcOfCircle CenterX=21.3 CenterY=-1.94 CenterZ=0 NormalX=0 NormalY=0 NormalZ=1 AngleXU=0 Radius=1 StartAngle=4.71239 EndAngle=6.28319
    g6: ArcOfCircle CenterX=21.3 CenterY=1.45 CenterZ=0 NormalX=0 NormalY=0 NormalZ=1 AngleXU=0 Radius=1 StartAngle=0 EndAngle=1.5708
    g7: ArcOfCircle CenterX=12.2 CenterY=1.45 CenterZ=0 NormalX=0 NormalY=0 NormalZ=1 AngleXU=0 Radius=1 StartAngle=1.5708 EndAngle=3.14159
    g8: GeomPoint [constr] X=11.2 Y=-2.94 Z=0
    g9: GeomPoint [constr] X=22.3 Y=2.45 Z=0
  constraints (24):
    c: Tangent(g0,g4) = -1.5708
    c: Tangent(g0,g5) = -1.5708
    c: Tangent(g1,g5) = -1.5708
    c: Tangent(g1,g6) = -1.5708
    c: Tangent(g2,g6) = -1.5708
    c: Tangent(g2,g7) = -1.5708
    c: Tangent(g3,g7) = -1.5708
    c: Tangent(g3,g4) = -1.5708
    c: Horizontal(g0)
    c: Horizontal(g2)
    c: Vertical(g1)
    c: Vertical(g3)
    c: Equal(g4,g5)
    c: Equal(g5,g6)
    c: Equal(g6,g7)
    c: PointOnObject(g8,g0)
    c: PointOnObject(g8,g3)
    c: PointOnObject(g9,g1)
    c: PointOnObject(g9,g2)
    c: Radius(g5) = 1
    c: DistanceY(g-3,g2) = 1
    c: DistanceX(g3,g-5) = 1
    c: DistanceX(g-6,g1) = 1
    c: DistanceY(g0,g-4) = 1
FEATURE [PartDesign::Pocket] Pocket016
  BaseFeature = -> Fillet047
  Direction = (0,0,1)
  Length = 0.5
  Length2 = 5
  Placement = pos=(0,0,0) rot=(1,0,0;1.5708rad)
  Profile = -> Sketch036
  ReferenceAxis = -> Sketch036 [N_Axis]
  Refine = true
  Suppressed = false
  Type = 0
FEATURE [Sketcher::SketchObject] Sketch037
  ArcFitTolerance = 1e-06
  AttachmentSupport = -> [Pocket007]
  ExternalGeometry = -> [Pocket007]
  FullyConstrained = true
  MakeInternals = false
  MapMode = 5
  Placement = pos=(0,-13.5,0) rot=(1,0,0;1.5708rad)
  sketch-geometry (8):
    g0: LineSegment StartX=0 StartY=65 StartZ=0 EndX=5 EndY=65 EndZ=0
    g1: LineSegment StartX=29 StartY=68 StartZ=0 EndX=33 EndY=71 EndZ=0
    g2: LineSegment StartX=0 StartY=65 StartZ=0 EndX=0 EndY=77 EndZ=0
    g3: LineSegment StartX=0 StartY=77 StartZ=0 EndX=33 EndY=77 EndZ=0
    g4: LineSegment StartX=33 StartY=77 StartZ=0 EndX=33 EndY=71 EndZ=0
    g5: ArcOfCircle CenterX=10 CenterY=65 CenterZ=0 NormalX=0 NormalY=0 NormalZ=1 AngleXU=0 Radius=5 StartAngle=1.5708 EndAngle=3.14159
    g6: ArcOfCircle CenterX=25 CenterY=65 CenterZ=0 NormalX=0 NormalY=0 NormalZ=1 AngleXU=0 Radius=5 StartAngle=0.643501 EndAngle=1.5708
    g7: LineSegment StartX=10 StartY=70 StartZ=0 EndX=25 EndY=70 EndZ=0
  constraints (20):
    c: Coincident(g0,g-4)
    c: Coincident(g0,g-4)
    c: Coincident(g1,g-5)
    c: Coincident(g2,g0)
    c: Vertical(g2)
    c: Coincident(g3,g2)
    c: Horizontal(g3)
    c: Coincident(g4,g3)
    c: Coincident(g4,g1)
    c: Vertical(g4)
    c: DistanceY(g2,g2) = 12
    c: Coincident(g5,g-3)
    c: Coincident(g5,g0)
    c: Coincident(g6,g-3)
    c: Coincident(g6,g1)
    c: Equal(g5,g-7)
    c: Equal(g-6,g6)
    c: Coincident(g1,g-6)
    c: Coincident(g7,g6)
    c: Coincident(g7,g5)
FEATURE [PartDesign::Pocket] Pocket017
  BaseFeature = -> Pocket007
  Direction = (0,1,-2e-16)
  Length = 5
  Length2 = 5
  Placement = pos=(0,0,0) rot=(1,0,0;1.5708rad)
  Profile = -> Sketch037
  ReferenceAxis = -> Sketch037 [N_Axis]
  Refine = true
  Suppressed = false
  Type = 1
FEATURE [Sketcher::SketchObject] Sketch038
  ArcFitTolerance = 1e-06
  AttachmentSupport = -> [Pocket016]
  ExternalGeometry = -> [Pocket016]
  FullyConstrained = true
  MakeInternals = false
  MapMode = 5
  Placement = pos=(0,-13.5,0) rot=(1,0,0;1.5708rad)
  sketch-geometry (7):
    g0: LineSegment StartX=33 StartY=71 StartZ=0 EndX=29 EndY=68 EndZ=0
    g1: LineSegment StartX=29 StartY=68 StartZ=0 EndX=5 EndY=65 EndZ=0
    g2: LineSegment StartX=5 StartY=65 StartZ=0 EndX=0 EndY=65 EndZ=0
    g3: LineSegment StartX=0 StartY=65 StartZ=0 EndX=0 EndY=11 EndZ=0
    g4: LineSegment StartX=0 StartY=11 StartZ=0 EndX=48 EndY=11 EndZ=0
    g5: LineSegment StartX=48 StartY=11 StartZ=0 EndX=48 EndY=71 EndZ=0
    g6: LineSegment StartX=48 StartY=71 StartZ=0 EndX=33 EndY=71 EndZ=0
  constraints (17):
    c: Coincident(g-3,g0)
    c: Coincident(g0,g-3)
    c: Coincident(g0,g1)
    c: Coincident(g1,g-4)
    c: Coincident(g1,g2)
    c: Coincident(g2,g-4)
    c: Coincident(g2,g3)
    c: Vertical(g3)
    c: Coincident(g3,g4)
    c: Horizontal(g4)
    c: Coincident(g4,g5)
    c: Vertical(g5)
    c: Coincident(g5,g6)
    c: Coincident(g6,g0)
    c: Horizontal(g6)
    c: DistanceX(g6,g6) = 15
    c: DistanceY(g5,g5) = 60
FEATURE [PartDesign::Pocket] Pocket018
  BaseFeature = -> Pocket016
  Direction = (0,1,-2e-16)
  Length = 5
  Length2 = 5
  Placement = pos=(0,0,0) rot=(1,0,0;1.5708rad)
  Profile = -> Sketch038
  ReferenceAxis = -> Sketch038 [N_Axis]
  Refine = true
  Suppressed = false
  Type = 1
FEATURE [PartDesign::Pocket] Pocket019
  BaseFeature = -> Pocket018
  Direction = (0,1,0)
  Length = 5
  Length2 = 5
  Placement = pos=(0,0,0) rot=(1,0,0;1.5708rad)
  Profile = -> Pocket018 [Face12]
  Refine = true
  Suppressed = false
  Type = 1
FEATURE [Sketcher::SketchObject] Sketch039
  ArcFitTolerance = 1e-06
  AttachmentSupport = -> [Pocket017]
  ExternalGeometry = -> [Pocket017]
  FullyConstrained = true
  MakeInternals = false
  MapMode = 5
  Placement = pos=(4.9738e-12,1.55e-14,70) rot=(0,0,1;3.14159rad)
  sketch-geometry (1):
    g0: Circle CenterX=-16.75 CenterY=0 CenterZ=0 NormalX=0 NormalY=0 NormalZ=1 AngleXU=0 Radius=12.5
  constraints (2):
    c: Coincident(g0,g-3)
    c: Diameter(g0) = 25
FEATURE [PartDesign::Pocket] Pocket020
  BaseFeature = -> Pocket017
  Direction = (-7.11e-14,0,-1)
  Length = 5
  Length2 = 5
  Placement = pos=(0,0,0) rot=(1,0,0;1.5708rad)
  Profile = -> Sketch039
  ReferenceAxis = -> Sketch039 [N_Axis]
  Refine = true
  Suppressed = false
  Type = 0
FEATURE [Sketcher::SketchObject] Sketch041
  ArcFitTolerance = 1e-06
  AttachmentSupport = -> [Pocket019]
  FullyConstrained = true
  MakeInternals = false
  MapMode = 5
  Placement = pos=(0,2.86e-14,65) rot=(1,0,0;3.14159rad)
  sketch-geometry (1):
    g0: Circle CenterX=16.75 CenterY=0 CenterZ=0 NormalX=0 NormalY=0 NormalZ=1 AngleXU=0 Radius=12.5
  constraints (3):
    c: PointOnObject(g0,g-1)
    c: Diameter(g0) = 25
    c: DistanceX(g-1,g0) = 16.75
FEATURE [PartDesign::Pocket] Pocket021
  BaseFeature = -> Pocket019
  Direction = (0,0,1)
  Length = 5
  Length2 = 5
  Placement = pos=(0,0,0) rot=(1,0,0;1.5708rad)
  Profile = -> Sketch041
  ReferenceAxis = -> Sketch041 [N_Axis]
  Refine = true
  Suppressed = false
  Type = 0
FEATURE [PartDesign::Body] Body002  label="Main-body001"
  AllowCompound = true
  Group = -> [Sketch031,Pad005,Fillet032,Fillet033,Sketch032,Pocket012,Sketch033,Pocket013,Sketch034,Pocket014,Sketch035,Pocket015,Fillet034,Fillet035,Fillet036,Fillet037,Fillet038,Fillet039,Fillet040,Fillet041,Fillet042,Fillet043,Fillet044,Fillet045,Fillet046,Fillet047,Sketch036,Pocket016,Sketch038,Pocket018,Pocket019,Sketch041,Pocket021]
  Origin = -> Origin002
  Tip = -> Pocket021
FEATURE [Sketcher::SketchObject] Sketch044
  ArcFitTolerance = 1e-06
  AttachmentSupport = -> [Pocket020]
  ExternalGeometry = -> [Pocket020]
  FullyConstrained = true
  MakeInternals = false
  MapMode = 5
  Placement = pos=(0,-13.5,0) rot=(1,0,0;1.5708rad)
  sketch-geometry (9):
    g0: LineSegment StartX=0 StartY=76.33 StartZ=0 EndX=0 EndY=64.7 EndZ=0
    g1: LineSegment StartX=0 StartY=64.7 StartZ=0 EndX=5.3 EndY=64.7 EndZ=0
    g2: LineSegment StartX=10.3 StartY=69.7 StartZ=0 EndX=24.7 EndY=69.7 EndZ=0
    g3: LineSegment StartX=28.94 StartY=67.58 StartZ=0 EndX=33.94 EndY=71.33 EndZ=0
    g4: LineSegment StartX=33.94 StartY=71.33 StartZ=0 EndX=33.94 EndY=76.33 EndZ=0
    g5: LineSegment StartX=33.94 StartY=76.33 StartZ=0 EndX=0 EndY=76.33 EndZ=0
    g6: ArcOfCircle CenterX=10.3 CenterY=64.7 CenterZ=0 NormalX=0 NormalY=0 NormalZ=1 AngleXU=0 Radius=5 StartAngle=1.5708 EndAngle=3.14159
    g7: ArcOfCircle CenterX=24.7 CenterY=64.4 CenterZ=0 NormalX=0 NormalY=0 NormalZ=1 AngleXU=0 Radius=5.3 StartAngle=0.643501 EndAngle=1.5708
    g8: GeomPoint X=29.18 Y=67.76 Z=0
  constraints (26):
    c: Vertical(g0)
    c: Coincident(g0,g1)
    c: Horizontal(g1)
    c: Horizontal(g2)
    c: Coincident(g3,g4)
    c: Vertical(g4)
    c: Coincident(g4,g5)
    c: Horizontal(g5)
    c: Coincident(g0,g5)
    c: Coincident(g6,g1)
    c: Coincident(g7,g3)
    c: PointOnObject(g0,g-2)
    c: DistanceY(g0,g-3) = 0.3
    c: DistanceX(g-6,g1) = 0.3
    c: DistanceY(g2,g-6) = 0.3
    c: Tangent(g6,g2) = 1.5708
    c: DistanceX(g-6,g2) = 0.3
    c: DistanceX(g2,g-5) = 0.3
    c: Tangent(g7,g2) = 1.5708
    c: PointOnObject(g8,g-4)
    c: Distance(g-5,g8) = 0.3
    c: PointOnObject(g8,g3)
    c: Distance(g8,g3) = 0.3
    c: DistanceX(g3,g3) = 5
    c: DistanceY(g4,g4) = 5
    c: Parallel(g3,g-7)
FEATURE [PartDesign::Pocket] Pocket022
  BaseFeature = -> Pocket020
  Direction = (0,1,-2e-16)
  Length = 5
  Length2 = 5
  Placement = pos=(0,0,0) rot=(1,0,0;1.5708rad)
  Profile = -> Sketch044
  ReferenceAxis = -> Sketch044 [N_Axis]
  Refine = true
  Suppressed = false
  Type = 1
FEATURE [PartDesign::Fillet] Fillet028
  Base = -> Fillet027 [Edge19]
  BaseFeature = -> Fillet027
  Placement = pos=(0,0,0) rot=(1,0,0;1.5708rad)
  Radius = 0.25
  Refine = true
  SupportTransform = false
  Suppressed = false
  UseAllEdges = false
FEATURE [PartDesign::Fillet] Fillet029
  Base = -> Fillet028 [Edge30,Edge23]
  BaseFeature = -> Fillet028
  Placement = pos=(0,0,0) rot=(1,0,0;1.5708rad)
  Radius = 0.25
  Refine = true
  SupportTransform = false
  Suppressed = false
  UseAllEdges = false
FEATURE [PartDesign::Fillet] Fillet030
  Base = -> Fillet029 [Edge358,Edge347]
  BaseFeature = -> Fillet029
  Placement = pos=(0,0,0) rot=(1,0,0;1.5708rad)
  Radius = 0.25
  Refine = true
  SupportTransform = false
  Suppressed = false
  UseAllEdges = false
FEATURE [PartDesign::Fillet] Fillet031
  Base = -> Fillet030 [Edge161]
  BaseFeature = -> Fillet030
  Placement = pos=(0,0,0) rot=(1,0,0;1.5708rad)
  Radius = 0.5
  Refine = true
  SupportTransform = false
  Suppressed = false
  UseAllEdges = false
FEATURE [Sketcher::SketchObject] Sketch040
  ArcFitTolerance = 1e-06
  AttachmentOffset = pos=(0,0,-24.5) rot=(0,0,1;0rad)
  AttachmentSupport = -> [Fillet031]
  ExternalGeometry = -> [Fillet031]
  FullyConstrained = true
  MakeInternals = false
  MapMode = 5
  Placement = pos=(0,1.78e-14,65) rot=(1,0,0;3.14159rad)
  sketch-geometry (1):
    g0: Circle CenterX=16.75 CenterY=0 CenterZ=0 NormalX=0 NormalY=0 NormalZ=1 AngleXU=0 Radius=12.5
  constraints (2):
    c: Diameter(g0) = 25
    c: Coincident(g0,g-3)
FEATURE [PartDesign::Pad] Pad006
  BaseFeature = -> Fillet031
  Direction = (0,0,-1)
  Length = 5
  Length2 = 10
  Placement = pos=(0,0,0) rot=(1,0,0;1.5708rad)
  Profile = -> Sketch040
  ReferenceAxis = -> Sketch040 [N_Axis]
  Refine = true
  Reversed = true
  Suppressed = false
  Type = 0
FEATURE [PartDesign::Fillet] Fillet048
  Base = -> Pad006 [Edge262,Edge199]
  BaseFeature = -> Pad006
  Placement = pos=(0,0,0) rot=(1,0,0;1.5708rad)
  Radius = 0.5
  Refine = true
  SupportTransform = false
  Suppressed = false
  UseAllEdges = false
FEATURE [Sketcher::SketchObject] Sketch042
  ArcFitTolerance = 1e-06
  AttachmentSupport = -> [XZ_Plane001]
  ExternalGeometry = -> [Fillet048]
  FullyConstrained = true
  MakeInternals = false
  MapMode = 5
  Placement = pos=(0,0,0) rot=(1,0,0;1.5708rad)
  sketch-geometry (8):
    g0: LineSegment StartX=27.6 StartY=70 StartZ=0 EndX=27.6 EndY=69.5 EndZ=0
    g1: LineSegment StartX=27.6 StartY=69.5 StartZ=0 EndX=28.75 EndY=69.5 EndZ=0
    g2: LineSegment StartX=28.75 StartY=69.5 StartZ=0 EndX=28.75 EndY=65.5 EndZ=0
    g3: LineSegment StartX=28.75 StartY=65.5 StartZ=0 EndX=27.6 EndY=65.5 EndZ=0
    g4: LineSegment StartX=27.6 StartY=65.5 StartZ=0 EndX=27.6 EndY=65 EndZ=0
    g5: LineSegment StartX=27.6 StartY=65 StartZ=0 EndX=29.25 EndY=65 EndZ=0
    g6: LineSegment StartX=29.25 StartY=65 StartZ=0 EndX=29.25 EndY=70 EndZ=0
    g7: LineSegment StartX=29.25 StartY=70 StartZ=0 EndX=27.6 EndY=70 EndZ=0
  constraints (24):
    c: PointOnObject(g0,g-4)
    c: Vertical(g0)
    c: Coincident(g0,g1)
    c: Horizontal(g1)
    c: Coincident(g1,g2)
    c: Vertical(g2)
    c: Coincident(g2,g3)
    c: Horizontal(g3)
    c: Coincident(g3,g4)
    c: PointOnObject(g4,g-5)
    c: Vertical(g4)
    c: Coincident(g4,g5)
    c: Horizontal(g5)
    c: Coincident(g5,g6)
    c: Vertical(g6)
    c: Coincident(g6,g7)
    c: Coincident(g7,g0)
    c: Horizontal(g7)
    c: PointOnObject(g-3,g6)
    c: DistanceY(g1,g6) = 0.5
    c: DistanceX(g1,g6) = 0.5
    c: DistanceY(g5,g2) = 0.5
    c: Vertical(g0,g-6)
    c: Vertical(g0,g3)
FEATURE [Sketcher::SketchObject] Sketch043
  ArcFitTolerance = 1e-06
  AttachmentSupport = -> [XZ_Plane001]
  ExternalGeometry = -> [Fillet048]
  FullyConstrained = true
  MakeInternals = false
  MapMode = 5
  Placement = pos=(0,0,0) rot=(1,0,0;1.5708rad)
  sketch-geometry (1):
    g0: LineSegment StartX=16.75 StartY=87 StartZ=0 EndX=16.75 EndY=67 EndZ=0
  constraints (3):
    c: Vertical(g0)
    c: Symmetric(g-3,g-3,g0)
    c: DistanceY(g0,g0) = 20
FEATURE [PartDesign::Groove] Groove
  Angle = 360
  Angle2 = 60
  Axis = (0,-2e-16,-1)
  Base = (16.75,1.93e-14,87)
  BaseFeature = -> Fillet048
  Placement = pos=(0,0,0) rot=(1,0,0;1.5708rad)
  Profile = -> Sketch042
  ReferenceAxis = -> Sketch043 [Edge1]
  Refine = true
  Suppressed = false
  Type = 0
FEATURE [PartDesign::Fillet] Fillet049
  Base = -> Groove [Edge377,Edge378]
  BaseFeature = -> Groove
  Placement = pos=(0,0,0) rot=(1,0,0;1.5708rad)
  Radius = 0.5
  Refine = true
  SupportTransform = false
  Suppressed = false
  UseAllEdges = false
FEATURE [Sketcher::SketchObject] Sketch045
  ArcFitTolerance = 1e-06
  AttachmentSupport = -> [XZ_Plane001]
  ExternalGeometry = -> [Fillet049]
  FullyConstrained = true
  MakeInternals = false
  MapMode = 5
  Placement = pos=(0,0,0) rot=(1,0,0;1.5708rad)
  sketch-geometry (9):
    g0: LineSegment StartX=19.3445 StartY=63.5 StartZ=0 EndX=22.8445 EndY=63.5 EndZ=0
    g1: LineSegment [constr] StartX=22.8445 StartY=63.5 StartZ=0 EndX=22.8445 EndY=64.3 EndZ=0
    g2: LineSegment [constr] StartX=22.8445 StartY=64.3 StartZ=0 EndX=19.3445 EndY=64.3 EndZ=0
    g3: LineSegment [constr] StartX=19.3445 StartY=64.3 StartZ=0 EndX=19.3445 EndY=63.5 EndZ=0
    g4: ArcOfCircle CenterX=19.5945 CenterY=64.05 CenterZ=0 NormalX=0 NormalY=0 NormalZ=1 AngleXU=0 Radius=0.25 StartAngle=1.5708 EndAngle=3.14159
    g5: ArcOfCircle CenterX=22.5945 CenterY=64.05 CenterZ=0 NormalX=0 NormalY=0 NormalZ=1 AngleXU=0 Radius=0.25 StartAngle=2.36e-14 EndAngle=1.5708
    g6: LineSegment StartX=19.3445 StartY=64.05 StartZ=0 EndX=19.3445 EndY=63.5 EndZ=0
    g7: LineSegment StartX=22.8445 StartY=64.05 StartZ=0 EndX=22.8445 EndY=63.5 EndZ=0
    g8: LineSegment StartX=22.5945 StartY=64.3 StartZ=0 EndX=19.5945 EndY=64.3 EndZ=0
  constraints (24):
    c: Coincident(g0,g1)
    c: Coincident(g1,g2)
    c: Coincident(g2,g3)
    c: Coincident(g3,g0)
    c: Horizontal(g0)
    c: Horizontal(g2)
    c: Vertical(g1)
    c: Vertical(g3)
    c: Distance(g1,g3) = 3.5
    c: Distance(g0,g2) = 0.8
    c: PointOnObject(g0,g-3)
    c: DistanceX(g0,g-3) = 0.5
    c: Tangent(g5,g2) = -1.5708
    c: Tangent(g4,g2) = -1.5708
    c: Tangent(g4,g3) = -1.5708
    c: Tangent(g5,g1) = -1.5708
    c: Equal(g4,g5)
    c: Radius(g4) = 0.25
    c: Coincident(g6,g4)
    c: Coincident(g7,g5)
    c: Coincident(g8,g5)
    c: Coincident(g8,g4)
    c: Coincident(g6,g0)
    c: Coincident(g7,g0)
FEATURE [PartDesign::Pocket] Pocket023
  BaseFeature = -> Fillet049
  Direction = (0,1,-2e-16)
  Length = 5
  Length2 = 5
  Placement = pos=(0,0,0) rot=(1,0,0;1.5708rad)
  Profile = -> Sketch045
  ReferenceAxis = -> Sketch045 [N_Axis]
  Refine = true
  Reversed = true
  Suppressed = false
  Type = 1
FEATURE [PartDesign::Fillet] Fillet050
  Base = -> Pocket023 [Edge17]
  BaseFeature = -> Pocket023
  Placement = pos=(0,0,0) rot=(1,0,0;1.5708rad)
  Radius = 0.125
  Refine = true
  SupportTransform = false
  Suppressed = false
  UseAllEdges = false
FEATURE [PartDesign::SubtractiveLoft] SubtractiveLoft002
  BaseFeature = -> Fillet050
  Closed = false
  Placement = pos=(0,0,0) rot=(1,0,0;1.5708rad)
  Profile = -> Fillet050 [Face190]
  Refine = true
  Ruled = false
  Sections = -> [Fillet050]
  Suppressed = false
FEATURE [PartDesign::Body] Body001  label="Core"
  AllowCompound = true
  Group = -> [Sketch003,Sketch004,Revolution,Pad001,Sketch012,Pocket004,Sketch013,Sketch015,Pad002,Pocket005,Sketch016,Pocket006,Sketch017,Sketch018,SubtractivePipe,SubtractiveLoft,Sketch019,Pad003,Sketch024,Revolution001,Sketch026,SubtractiveLoft001,Sketch027,Sketch028,Pad004,Pocket008,Pocket009,Fillet016,Fillet017,Fillet018,Fillet019,Fillet020,Fillet021,Sketch029,Pocket010,Fillet022,Sketch030,Pocket011,+20 more]
  Origin = -> Origin001
  Tip = -> SubtractiveLoft002
FEATURE [Sketcher::SketchObject] Sketch046
  ArcFitTolerance = 1e-06
  AttachmentSupport = -> [Pocket022]
  FullyConstrained = true
  MakeInternals = false
  MapMode = 5
  Placement = pos=(0,2.5,0) rot=(1,0,0;1.5708rad)
  sketch-geometry (4):
    g0: LineSegment StartX=18.5 StartY=30 StartZ=0 EndX=18.5 EndY=33.5 EndZ=0
    g1: LineSegment StartX=18.5 StartY=33.5 StartZ=0 EndX=15 EndY=33.5 EndZ=0
    g2: LineSegment StartX=15 StartY=33.5 StartZ=0 EndX=15 EndY=30 EndZ=0
    g3: LineSegment StartX=15 StartY=30 StartZ=0 EndX=18.5 EndY=30 EndZ=0
  constraints (12):
    c: Coincident(g0,g1)
    c: Coincident(g1,g2)
    c: Coincident(g2,g3)
    c: Coincident(g3,g0)
    c: Vertical(g0)
    c: Vertical(g2)
    c: Horizontal(g1)
    c: Horizontal(g3)
    c: Distance(g0,g2) = 3.5
    c: Distance(g1,g3) = 3.5
    c: DistanceY(g-1,g2) = 30
    c: DistanceX(g-1,g2) = 15
FEATURE [PartDesign::Pocket] Pocket024
  BaseFeature = -> Pocket022
  Direction = (0,1,-2e-16)
  Length = 10
  Length2 = 5
  Placement = pos=(0,0,0) rot=(1,0,0;1.5708rad)
  Profile = -> Sketch046
  ReferenceAxis = -> Sketch046 [N_Axis]
  Refine = true
  Suppressed = false
  Type = 0
FEATURE [PartDesign::Fillet] Fillet051
  Base = -> Pocket024 [Edge276,Edge278,Edge280,Edge275]
  BaseFeature = -> Pocket024
  Placement = pos=(0,0,0) rot=(1,0,0;1.5708rad)
  Radius = 1
  Refine = true
  SupportTransform = false
  Suppressed = false
  UseAllEdges = false
FEATURE [PartDesign::Body] Body  label="Main-body"
  AllowCompound = true
  Group = -> [Sketch,Pad,Fillet,Fillet001,Sketch006,Pocket,Sketch008,Pocket001,Sketch009,Pocket002,Sketch010,Pocket003,Fillet002,Fillet003,Fillet004,Fillet005,Fillet006,Fillet007,Fillet008,Fillet009,Fillet010,Fillet011,Fillet012,Fillet013,Fillet014,Fillet015,Sketch021,Pocket007,Sketch037,Pocket017,Sketch039,Pocket020,Sketch044,Pocket022,Sketch046,Pocket024,Fillet051]
  Origin = -> Origin
  Tip = -> Fillet051
